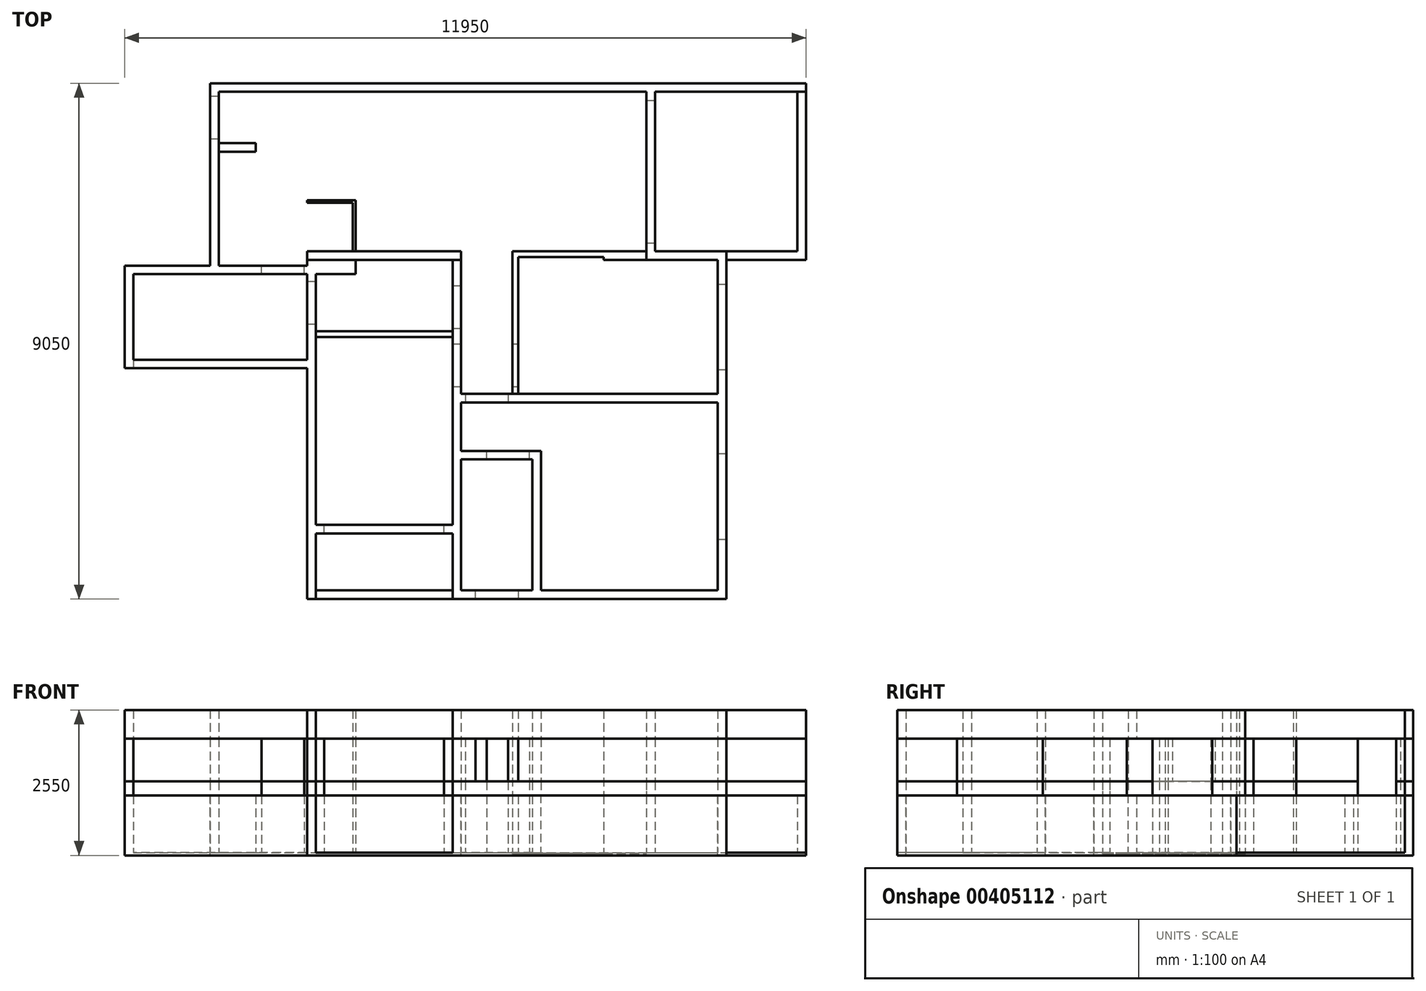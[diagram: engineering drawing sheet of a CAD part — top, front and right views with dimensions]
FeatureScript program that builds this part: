
annotation { "Feature Type Name" : "Feature", "Feature Type Description" : "" }
export const myFeature = defineFeature(function(context is Context, id is Id, definition is map)
    precondition{}
    {
        {
            var Q0;
            Q0=qCreatedBy(makeId("Top.planeOp"),FACE);
            var sketch = newSketch(context, id + "F0", { "sketchPlane" : qUnion([Q0])});
            skLineSegment(sketch, "E0.bottom", {"start": v(-5150, 2800) * mm, "end": v(2350, 2800) * mm});
            skLineSegment(sketch, "E0.top", {"start": v(-3600, 0) * mm, "end": v(-900, 0) * mm});
            skLineSegment(sketch, "E0.left", {"start": v(-5150, 2800) * mm, "end": v(-5150, 0) * mm});
            skLineSegment(sketch, "E0.right", {"start": v(5000, 2800) * mm, "end": v(5000, 0) * mm});
            skLineSegment(sketch, "E1.bottom", {"start": v(-5300, 2950) * mm, "end": v(5150, 2950) * mm});
            skLineSegment(sketch, "E1.top", {"start": v(-5300, -150) * mm, "end": v(-5150, -150) * mm});
            skLineSegment(sketch, "E1.left", {"start": v(-5300, 2950) * mm, "end": v(-5300, -150) * mm});
            skLineSegment(sketch, "E1.right", {"start": v(5150, 2950) * mm, "end": v(5150, -150) * mm});
            skLineSegment(sketch, "E2.top", {"start": v(2350, 2650) * mm, "end": v(2500, 2650) * mm});
            skLineSegment(sketch, "E2.left", {"start": v(2350, 2800) * mm, "end": v(2350, 2650) * mm});
            skLineSegment(sketch, "E2.right", {"start": v(2500, 2800) * mm, "end": v(2500, 2650) * mm});
            skLineSegment(sketch, "E3.top", {"start": v(2350, 150) * mm, "end": v(2500, 150) * mm});
            skLineSegment(sketch, "E3.left", {"start": v(2350, 2650) * mm, "end": v(2350, 150) * mm});
            skLineSegment(sketch, "E3.right", {"start": v(2500, 2650) * mm, "end": v(2500, 150) * mm});
            skLineSegment(sketch, "E4.left", {"start": v(2350, 150) * mm, "end": v(2350, 0) * mm});
            skLineSegment(sketch, "E4.right", {"start": v(2500, 150) * mm, "end": v(2500, 0) * mm});
            skLineSegment(sketch, "E5.bottom", {"start": v(0, 0) * mm, "end": v(2350, 0) * mm});
            skLineSegment(sketch, "E5.top", {"start": v(0, -2650) * mm, "end": v(3600, -2650) * mm});
            skLineSegment(sketch, "E5.left", {"start": v(0, 0) * mm, "end": v(0, -2650) * mm});
            skLineSegment(sketch, "E5.right", {"start": v(3750, 0) * mm, "end": v(3750, -2650) * mm});
            skLineSegment(sketch, "E6.bottom", {"start": v(100, -2500) * mm, "end": v(3600, -2500) * mm});
            skLineSegment(sketch, "E6.top", {"start": v(100, -100) * mm, "end": v(1600, -100) * mm});
            skLineSegment(sketch, "E6.left", {"start": v(100, -2500) * mm, "end": v(100, -100) * mm});
            skLineSegment(sketch, "E6.right", {"start": v(3600, -2500) * mm, "end": v(3600, -150) * mm});
            skLineSegment(sketch, "E7", {"start": v(1600, -100) * mm, "end": v(1600, -150) * mm});
            skLineSegment(sketch, "E8.trimOffspring", {"start": v(1600, -150) * mm, "end": v(3600, -150) * mm});
            skLineSegment(sketch, "E9.trimOffspring", {"start": v(2500, 2800) * mm, "end": v(5000, 2800) * mm});
            skLineSegment(sketch, "E10.trimOffspring", {"start": v(2500, 0) * mm, "end": v(3750, 0) * mm});
            skLineSegment(sketch, "E11.trimOffspring", {"start": v(2500, 0) * mm, "end": v(5000, 0) * mm});
            skLineSegment(sketch, "E12.trimOffspring", {"start": v(3750, -150) * mm, "end": v(5150, -150) * mm});
            skLineSegment(sketch, "E13.bottom", {"start": v(3600, -2500) * mm, "end": v(-1050, -2500) * mm});
            skLineSegment(sketch, "E13.top", {"start": v(3750, -6100) * mm, "end": v(-1050, -6100) * mm});
            skLineSegment(sketch, "E13.left", {"start": v(3750, -2500) * mm, "end": v(3750, -6100) * mm});
            skLineSegment(sketch, "E13.right", {"start": v(-1050, -2500) * mm, "end": v(-1050, -4800) * mm});
            skLineSegment(sketch, "E14.bottom", {"start": v(3600, -2650) * mm, "end": v(-900, -2650) * mm});
            skLineSegment(sketch, "E14.top", {"start": v(3600, -5950) * mm, "end": v(-900, -5950) * mm});
            skLineSegment(sketch, "E14.left", {"start": v(3600, -2650) * mm, "end": v(3600, -5950) * mm});
            skLineSegment(sketch, "E14.right", {"start": v(-900, -2650) * mm, "end": v(-900, -5950) * mm});
            skLineSegment(sketch, "E15.bottom", {"start": v(-900, -6100) * mm, "end": v(-3600, -6100) * mm});
            skLineSegment(sketch, "E15.top", {"start": v(-900, 0) * mm, "end": v(-3600, 0) * mm});
            skLineSegment(sketch, "E15.left", {"start": v(-900, -6100) * mm, "end": v(-900, 0) * mm});
            skLineSegment(sketch, "E15.right", {"start": v(-3600, -6100) * mm, "end": v(-3600, 0) * mm});
            skLineSegment(sketch, "E16.bottom", {"start": v(-1050, -5950) * mm, "end": v(-3450, -5950) * mm});
            skLineSegment(sketch, "E16.top", {"start": v(-1050, -150) * mm, "end": v(-3450, -150) * mm});
            skLineSegment(sketch, "E16.left", {"start": v(-1050, -5950) * mm, "end": v(-1050, -4950) * mm});
            skLineSegment(sketch, "E16.right", {"start": v(-3450, -5950) * mm, "end": v(-3450, -4950) * mm});
            skLineSegment(sketch, "E17.bottom", {"start": v(-1050, -1400) * mm, "end": v(-3450, -1400) * mm});
            skLineSegment(sketch, "E17.top", {"start": v(-1050, -1500) * mm, "end": v(-3450, -1500) * mm});
            skLineSegment(sketch, "E17.left", {"start": v(-1050, -1400) * mm, "end": v(-1050, -1500) * mm});
            skLineSegment(sketch, "E17.right", {"start": v(-3450, -1400) * mm, "end": v(-3450, -1500) * mm});
            skLineSegment(sketch, "E18.bottom", {"start": v(-3450, -4950) * mm, "end": v(-3300, -4950) * mm});
            skLineSegment(sketch, "E18.top", {"start": v(-3450, -4800) * mm, "end": v(-3300, -4800) * mm});
            skLineSegment(sketch, "E18.right", {"start": v(-3300, -4950) * mm, "end": v(-3300, -4800) * mm});
            skLineSegment(sketch, "E19.bottom", {"start": v(-3300, -4950) * mm, "end": v(-1200, -4950) * mm});
            skLineSegment(sketch, "E19.top", {"start": v(-3300, -4800) * mm, "end": v(-1200, -4800) * mm});
            skLineSegment(sketch, "E19.right", {"start": v(-1200, -4950) * mm, "end": v(-1200, -4800) * mm});
            skLineSegment(sketch, "E20.bottom", {"start": v(-1200, -4950) * mm, "end": v(-1050, -4950) * mm});
            skLineSegment(sketch, "E20.top", {"start": v(-1200, -4800) * mm, "end": v(-1050, -4800) * mm});
            skLineSegment(sketch, "E21.trimOffspring", {"start": v(-3450, -4800) * mm, "end": v(-3450, -150) * mm});
            skLineSegment(sketch, "E22.trimOffspring", {"start": v(-1050, -4950) * mm, "end": v(-1050, -6100) * mm});
            skLineSegment(sketch, "E23.trimOffspring", {"start": v(-1050, -4800) * mm, "end": v(-1050, -150) * mm});
            skLineSegment(sketch, "E24.trimOffspring", {"start": v(0, -150) * mm, "end": v(100, -150) * mm});
            skLineSegment(sketch, "E25.bottom", {"start": v(-5150, 1750) * mm, "end": v(-4500, 1750) * mm});
            skLineSegment(sketch, "E25.top", {"start": v(-5150, -250) * mm, "end": v(-2750, -250) * mm});
            skLineSegment(sketch, "E25.left", {"start": v(-5150, 1750) * mm, "end": v(-5150, -250) * mm});
            skLineSegment(sketch, "E25.right", {"start": v(-2750, 1750) * mm, "end": v(-2750, -250) * mm});
            skLineSegment(sketch, "E26.bottom", {"start": v(-5300, 1900) * mm, "end": v(-2750, 1900) * mm});
            skLineSegment(sketch, "E26.top", {"start": v(-5300, -400) * mm, "end": v(-2750, -400) * mm});
            skLineSegment(sketch, "E26.left", {"start": v(-5300, 1900) * mm, "end": v(-5300, -400) * mm});
            skLineSegment(sketch, "E26.right", {"start": v(-2750, 1900) * mm, "end": v(-2750, -400) * mm});
            skLineSegment(sketch, "E27", {"start": v(-4500, 1750) * mm, "end": v(-4500, 1900) * mm});
            skLineSegment(sketch, "E28.trimOffspring", {"start": v(-3600, -150) * mm, "end": v(-900, -150) * mm});
            skLineSegment(sketch, "E29.bottom", {"start": v(-3600, -400) * mm, "end": v(-6650, -400) * mm});
            skLineSegment(sketch, "E29.top", {"start": v(-3600, -1900) * mm, "end": v(-6650, -1900) * mm});
            skLineSegment(sketch, "E29.left", {"start": v(-3600, -400) * mm, "end": v(-3600, -1900) * mm});
            skLineSegment(sketch, "E29.right", {"start": v(-6650, -400) * mm, "end": v(-6650, -1900) * mm});
            skLineSegment(sketch, "E30.bottom", {"start": v(-3600, -400) * mm, "end": v(-6800, -400) * mm});
            skLineSegment(sketch, "E30.top", {"start": v(-3600, -2050) * mm, "end": v(-6800, -2050) * mm});
            skLineSegment(sketch, "E30.left", {"start": v(-3600, -400) * mm, "end": v(-3600, -2050) * mm});
            skLineSegment(sketch, "E30.right", {"start": v(-6800, -400) * mm, "end": v(-6800, -2050) * mm});
            skLineSegment(sketch, "E31", {"start": v(-2750, 900) * mm, "end": v(-3600, 900) * mm});
            skLineSegment(sketch, "E32", {"start": v(-3600, 900) * mm, "end": v(-3600, 850) * mm});
            skLineSegment(sketch, "E33", {"start": v(-3600, 850) * mm, "end": v(-2800, 850) * mm});
            skLineSegment(sketch, "E34", {"start": v(-2800, 850) * mm, "end": v(-2800, 0) * mm});
            skLineSegment(sketch, "E35.bottom", {"start": v(-900, -5950) * mm, "end": v(350, -5950) * mm});
            skLineSegment(sketch, "E35.top", {"start": v(-900, -3650) * mm, "end": v(350, -3650) * mm});
            skLineSegment(sketch, "E35.left", {"start": v(-900, -5950) * mm, "end": v(-900, -3650) * mm});
            skLineSegment(sketch, "E35.right", {"start": v(350, -5950) * mm, "end": v(350, -3650) * mm});
            skLineSegment(sketch, "E36.bottom", {"start": v(-900, -5950) * mm, "end": v(500, -5950) * mm});
            skLineSegment(sketch, "E36.top", {"start": v(-900, -3500) * mm, "end": v(500, -3500) * mm});
            skLineSegment(sketch, "E36.left", {"start": v(-900, -5950) * mm, "end": v(-900, -3500) * mm});
            skLineSegment(sketch, "E36.right", {"start": v(500, -5950) * mm, "end": v(500, -3500) * mm});
            skLineSegment(sketch, "E37", {"start": v(2350, 0) * mm, "end": v(2350, -150) * mm});
            skLineSegment(sketch, "E38", {"start": v(5000, 2800) * mm, "end": v(5150, 2800) * mm});
            skLineSegment(sketch, "E39.bottom", {"start": v(-6800, -400) * mm, "end": v(-5300, -400) * mm});
            skLineSegment(sketch, "E39.top", {"start": v(-6800, -250) * mm, "end": v(-5300, -250) * mm});
            skLineSegment(sketch, "E39.left", {"start": v(-6800, -400) * mm, "end": v(-6800, -250) * mm});
            skLineSegment(sketch, "E39.right", {"start": v(-5300, -400) * mm, "end": v(-5300, -250) * mm});
            skLineSegment(sketch, "E40", {"start": v(-3450, -5950) * mm, "end": v(-3450, -6100) * mm});
            skLineSegment(sketch, "E41", {"start": v(-6650, -1900) * mm, "end": v(-6650, -2050) * mm});
            skLineSegment(sketch, "E42", {"start": v(3600, -5050) * mm, "end": v(3750, -5050) * mm});
            skLineSegment(sketch, "E43", {"start": v(3600, -3550) * mm, "end": v(3750, -3550) * mm});
            skLineSegment(sketch, "E44", {"start": v(3600, -575) * mm, "end": v(3750, -575) * mm});
            skLineSegment(sketch, "E45", {"start": v(3600, -2075) * mm, "end": v(3750, -2075) * mm});
            skLineSegment(sketch, "E46", {"start": v(3600, -4300) * mm, "end": v(3750, -4300) * mm, "construction": true});
            skLineSegment(sketch, "E47", {"start": v(3600, -1325) * mm, "end": v(3750, -1325) * mm, "construction": true});
            skLineSegment(sketch, "E48", {"start": v(-825, -2500) * mm, "end": v(-825, -2650) * mm});
            skLineSegment(sketch, "E49", {"start": v(-75, -2500) * mm, "end": v(-75, -2650) * mm});
            skLineSegment(sketch, "E50", {"start": v(-450, -2500) * mm, "end": v(-450, -2650) * mm, "construction": true});
            skLineSegment(sketch, "E51", {"start": v(300, -3650) * mm, "end": v(300, -3500) * mm});
            skLineSegment(sketch, "E52", {"start": v(-450, -3650) * mm, "end": v(-450, -3500) * mm});
            skLineSegment(sketch, "E53", {"start": v(-1050, -1625) * mm, "end": v(-900, -1625) * mm});
            skLineSegment(sketch, "E54", {"start": v(-1050, -2375) * mm, "end": v(-900, -2375) * mm});
            skLineSegment(sketch, "E55", {"start": v(-1050, -1350) * mm, "end": v(-900, -1350) * mm});
            skLineSegment(sketch, "E56", {"start": v(-1050, -600) * mm, "end": v(-900, -600) * mm});
            skLineSegment(sketch, "E57", {"start": v(-3600, -525) * mm, "end": v(-3450, -525) * mm});
            skLineSegment(sketch, "E58", {"start": v(-3600, -1275) * mm, "end": v(-3450, -1275) * mm});
            skLineSegment(sketch, "E59", {"start": v(-650, -6100) * mm, "end": v(-650, -5950) * mm});
            skLineSegment(sketch, "E60", {"start": v(-3600, -900) * mm, "end": v(-3450, -900) * mm, "construction": true});
            skLineSegment(sketch, "E61", {"start": v(-275, -5950) * mm, "end": v(-275, -6100) * mm, "construction": true});
            skLineSegment(sketch, "E62", {"start": v(100, -5950) * mm, "end": v(100, -6100) * mm});
            skLineSegment(sketch, "E63", {"start": v(-5300, 1975) * mm, "end": v(-5150, 1975) * mm});
            skLineSegment(sketch, "E64", {"start": v(-5300, 2725) * mm, "end": v(-5150, 2725) * mm});
            skLineSegment(sketch, "E65", {"start": v(-5300, 2350) * mm, "end": v(-5150, 2350) * mm, "construction": true});
            skLineSegment(sketch, "E66", {"start": v(0, -2375) * mm, "end": v(100, -2375) * mm});
            skLineSegment(sketch, "E67", {"start": v(0, -1625) * mm, "end": v(100, -1625) * mm});
            skLineSegment(sketch, "E68", {"start": v(-3650, -400) * mm, "end": v(-3650, -250) * mm});
            skLineSegment(sketch, "E69", {"start": v(-4400, -400) * mm, "end": v(-4400, -250) * mm});
            skLineSegment(sketch, "E70", {"start": v(-1050, -2000) * mm, "end": v(-900, -2000) * mm, "construction": true});
            skSolve(sketch);
        }
        {
            var Q0;
            {var subQ1=sQuery(id+"F0.wireOp",EDGE,"E14.top");Q0=makeQuery(id+"F0.imprint","IMPRINT",FACE,{"disambiguationData":[TD([[makeQuery(id+"F0.imprint","IMPRINT",EDGE,{"derivedFrom":subQ1}),1.0]])]});}
            var Q1;
            {var subQ0=sQuery(id+"F0.wireOp",EDGE,"E42");Q1=makeQuery(id+"F0.imprint","IMPRINT",FACE,{"disambiguationData":[TD([[makeQuery(id+"F0.imprint","IMPRINT",EDGE,{"derivedFrom":subQ0}),1.0]])]});}
            var Q2;
            {var subQ7=sQuery(id+"F0.wireOp",EDGE,"E43");Q2=makeQuery(id+"F0.imprint","IMPRINT",FACE,{"disambiguationData":[TD([[makeQuery(id+"F0.imprint","IMPRINT",EDGE,{"derivedFrom":subQ7}),1.0]])]});}
            var Q3;
            {var subQ1=sQuery(id+"F0.wireOp",EDGE,"E14.top");Q3=makeQuery(id+"F0.imprint","IMPRINT",FACE,{"disambiguationData":[TD([[makeQuery(id+"F0.imprint","IMPRINT",EDGE,{"derivedFrom":subQ1}),-1.0]])]});}
            var Q4;
            {var subQ3=sQuery(id+"F0.wireOp",EDGE,"E35.right");Q4=makeQuery(id+"F0.imprint","IMPRINT",FACE,{"disambiguationData":[TD([[makeQuery(id+"F0.imprint","IMPRINT",EDGE,{"derivedFrom":subQ3}),-1.0]])]});}
            var Q5;
            {var subQ0=sQuery(id+"F0.wireOp",EDGE,"E51");Q5=makeQuery(id+"F0.imprint","IMPRINT",FACE,{"disambiguationData":[TD([[makeQuery(id+"F0.imprint","IMPRINT",EDGE,{"derivedFrom":subQ0}),1.0]])]});}
            var Q6;
            {var subQ3=sQuery(id+"F0.wireOp",EDGE,"E52");Q6=makeQuery(id+"F0.imprint","IMPRINT",FACE,{"disambiguationData":[TD([[makeQuery(id+"F0.imprint","IMPRINT",EDGE,{"derivedFrom":subQ3}),1.0]])]});}
            var Q7;
            {var subQ0=sQuery(id+"F0.wireOp",EDGE,"E59");Q7=makeQuery(id+"F0.imprint","IMPRINT",FACE,{"disambiguationData":[TD([[makeQuery(id+"F0.imprint","IMPRINT",EDGE,{"derivedFrom":subQ0}),-1.0]])]});}
            var Q8;
            {var subQ3=sQuery(id+"F0.wireOp",EDGE,"E59");Q8=makeQuery(id+"F0.imprint","IMPRINT",FACE,{"disambiguationData":[TD([[makeQuery(id+"F0.imprint","IMPRINT",EDGE,{"derivedFrom":subQ3}),1.0]])]});}
            var Q9;
            {var subQ2=sQuery(id+"F0.wireOp",EDGE,"E20.bottom");Q9=makeQuery(id+"F0.imprint","IMPRINT",FACE,{"disambiguationData":[TD([[makeQuery(id+"F0.imprint","IMPRINT",EDGE,{"derivedFrom":subQ2}),1.0]])]});}
            var Q10;
            Q10=makeQuery(id+"F0.imprint","IMPRINT",FACE,{"disambiguationData":[TD([[makeQuery(id+"F0.imprint","IMPRINT",EDGE,{"derivedFrom":sQuery(id+"F0.wireOp",EDGE,"E19.bottom")}),1.0]])]});
            var Q11;
            Q11=makeQuery(id+"F0.imprint","IMPRINT",FACE,{"disambiguationData":[TD([[makeQuery(id+"F0.imprint","IMPRINT",EDGE,{"derivedFrom":sQuery(id+"F0.wireOp",EDGE,"E16.right")}),1.0]])]});
            var Q12;
            {var subQ4=sQuery(id+"F0.wireOp",EDGE,"E17.top");Q12=makeQuery(id+"F0.imprint","IMPRINT",FACE,{"disambiguationData":[TD([[makeQuery(id+"F0.imprint","IMPRINT",EDGE,{"derivedFrom":subQ4}),1.0]])]});}
            var Q13;
            {var subQ5=sQuery(id+"F0.wireOp",EDGE,"E54");Q13=makeQuery(id+"F0.imprint","IMPRINT",FACE,{"disambiguationData":[TD([[makeQuery(id+"F0.imprint","IMPRINT",EDGE,{"derivedFrom":subQ5}),-1.0]])]});}
            var Q14;
            {var subQ0=sQuery(id+"F0.wireOp",EDGE,"E48");Q14=makeQuery(id+"F0.imprint","IMPRINT",FACE,{"disambiguationData":[TD([[makeQuery(id+"F0.imprint","IMPRINT",EDGE,{"derivedFrom":subQ0}),-1.0]])]});}
            var Q15;
            {var subQ0=sQuery(id+"F0.wireOp",EDGE,"E48");Q15=makeQuery(id+"F0.imprint","IMPRINT",FACE,{"disambiguationData":[TD([[makeQuery(id+"F0.imprint","IMPRINT",EDGE,{"derivedFrom":subQ0}),1.0]])]});}
            var Q16;
            {var subQ5=sQuery(id+"F0.wireOp",EDGE,"E49");Q16=makeQuery(id+"F0.imprint","IMPRINT",FACE,{"disambiguationData":[TD([[makeQuery(id+"F0.imprint","IMPRINT",EDGE,{"derivedFrom":subQ5}),1.0]])]});}
            var Q17;
            {var subQ0=sQuery(id+"F0.wireOp",EDGE,"E53");Q17=makeQuery(id+"F0.imprint","IMPRINT",FACE,{"disambiguationData":[TD([[makeQuery(id+"F0.imprint","IMPRINT",EDGE,{"derivedFrom":subQ0}),-1.0]])]});}
            var Q18;
            {var subQ4=sQuery(id+"F0.wireOp",EDGE,"E53");Q18=makeQuery(id+"F0.imprint","IMPRINT",FACE,{"disambiguationData":[TD([[makeQuery(id+"F0.imprint","IMPRINT",EDGE,{"derivedFrom":subQ4}),1.0]])]});}
            var Q19;
            {var subQ0=sQuery(id+"F0.wireOp",EDGE,"E55");Q19=makeQuery(id+"F0.imprint","IMPRINT",FACE,{"disambiguationData":[TD([[makeQuery(id+"F0.imprint","IMPRINT",EDGE,{"derivedFrom":subQ0}),1.0]])]});}
            var Q20;
            {var subQ0=sQuery(id+"F0.wireOp",EDGE,"E17.bottom");Q20=makeQuery(id+"F0.imprint","IMPRINT",FACE,{"disambiguationData":[TD([[makeQuery(id+"F0.imprint","IMPRINT",EDGE,{"derivedFrom":subQ0}),1.0]])]});}
            var Q21;
            {var subQ3=sQuery(id+"F0.wireOp",EDGE,"E56");Q21=makeQuery(id+"F0.imprint","IMPRINT",FACE,{"disambiguationData":[TD([[makeQuery(id+"F0.imprint","IMPRINT",EDGE,{"derivedFrom":subQ3}),1.0]])]});}
            var Q22;
            {var subQ1=sQuery(id+"F0.wireOp",EDGE,"E15.top");var subQ5=sQuery(id+"F0.wireOp",EDGE,"E15.left");var subQ6=makeQuery(id+"F0.imprint","INTERSECT",VERTEX,{"derivedFrom":[subQ1,subQ5]});Q22=makeQuery(id+"F0.imprint","IMPRINT",FACE,{"disambiguationData":[TD([[makeQuery(id+"F0.imprint","IMPRINT",EDGE,{"disambiguationData":[TD([[subQ6,-1.0]])],"derivedFrom":subQ1}),1.0]])]});}
            var Q23;
            {var subQ0=sQuery(id+"F0.wireOp",EDGE,"E57");Q23=makeQuery(id+"F0.imprint","IMPRINT",FACE,{"disambiguationData":[TD([[makeQuery(id+"F0.imprint","IMPRINT",EDGE,{"derivedFrom":subQ0}),-1.0]])]});}
            var Q24;
            {var subQ0=sQuery(id+"F0.wireOp",EDGE,"E57");Q24=makeQuery(id+"F0.imprint","IMPRINT",FACE,{"disambiguationData":[TD([[makeQuery(id+"F0.imprint","IMPRINT",EDGE,{"derivedFrom":subQ0}),1.0]])]});}
            var Q25;
            {var subQ0=sQuery(id+"F0.wireOp",EDGE,"E26.top");var subQ5=sQuery(id+"F0.wireOp",EDGE,"E21.trimOffspring");var subQ6=makeQuery(id+"F0.imprint","INTERSECT",VERTEX,{"derivedFrom":[subQ5,subQ0]});Q25=makeQuery(id+"F0.imprint","IMPRINT",FACE,{"disambiguationData":[TD([[makeQuery(id+"F0.imprint","IMPRINT",EDGE,{"disambiguationData":[TD([[subQ6,-1.0]])],"derivedFrom":subQ5}),1.0]])]});}
            var Q26;
            {var subQ0=sQuery(id+"F0.wireOp",EDGE,"E26.top");var subQ1=sQuery(id+"F0.wireOp",EDGE,"E21.trimOffspring");var subQ2=makeQuery(id+"F0.imprint","INTERSECT",VERTEX,{"derivedFrom":[subQ1,subQ0]});Q26=makeQuery(id+"F0.imprint","IMPRINT",FACE,{"disambiguationData":[TD([[makeQuery(id+"F0.imprint","IMPRINT",EDGE,{"disambiguationData":[TD([[subQ2,-1.0]])],"derivedFrom":subQ1}),-1.0]])]});}
            var Q27;
            {var subQ0=sQuery(id+"F0.wireOp",EDGE,"E28.trimOffspring");var subQ1=sQuery(id+"F0.wireOp",EDGE,"E21.trimOffspring");var subQ2=makeQuery(id+"F0.imprint","INTERSECT",VERTEX,{"derivedFrom":[subQ1,subQ0]});Q27=makeQuery(id+"F0.imprint","IMPRINT",FACE,{"disambiguationData":[TD([[makeQuery(id+"F0.imprint","IMPRINT",EDGE,{"disambiguationData":[TD([[subQ2,1.0]])],"derivedFrom":subQ1}),-1.0]])]});}
            var Q28;
            {var subQ1=sQuery(id+"F0.wireOp",EDGE,"E15.top");var subQ8=makeQuery(id+"F0.imprint","INTERSECT",VERTEX,{"derivedFrom":[subQ1,sQuery(id+"F0.wireOp",EDGE,"E34")]});Q28=makeQuery(id+"F0.imprint","IMPRINT",FACE,{"disambiguationData":[TD([[makeQuery(id+"F0.imprint","IMPRINT",EDGE,{"disambiguationData":[TD([[subQ8,1.0]])],"derivedFrom":subQ1}),1.0]])]});}
            var Q29;
            {var subQ0=sQuery(id+"F0.wireOp",EDGE,"E28.trimOffspring");var subQ1=sQuery(id+"F0.wireOp",EDGE,"E15.right");var subQ2=makeQuery(id+"F0.imprint","INTERSECT",VERTEX,{"derivedFrom":[subQ1,subQ0]});Q29=makeQuery(id+"F0.imprint","IMPRINT",FACE,{"disambiguationData":[TD([[makeQuery(id+"F0.imprint","IMPRINT",EDGE,{"disambiguationData":[TD([[subQ2,1.0]])],"derivedFrom":subQ1}),-1.0]])]});}
            var Q30;
            {var subQ1=sQuery(id+"F0.wireOp",EDGE,"E1.top");Q30=makeQuery(id+"F0.imprint","IMPRINT",FACE,{"disambiguationData":[TD([[makeQuery(id+"F0.imprint","IMPRINT",EDGE,{"derivedFrom":subQ1}),-1.0]])]});}
            var Q31;
            Q31=makeQuery(id+"F0.imprint","IMPRINT",FACE,{"disambiguationData":[TD([[makeQuery(id+"F0.imprint","IMPRINT",EDGE,{"derivedFrom":sQuery(id+"F0.wireOp",EDGE,"E39.top")}),-1.0]])]});
            var Q32;
            {var subQ1=sQuery(id+"F0.wireOp",EDGE,"E29.right");Q32=makeQuery(id+"F0.imprint","IMPRINT",FACE,{"disambiguationData":[TD([[makeQuery(id+"F0.imprint","IMPRINT",EDGE,{"derivedFrom":subQ1}),-1.0]])]});}
            var Q33;
            {var subQ1=sQuery(id+"F0.wireOp",EDGE,"E1.top");Q33=makeQuery(id+"F0.imprint","IMPRINT",FACE,{"disambiguationData":[TD([[makeQuery(id+"F0.imprint","IMPRINT",EDGE,{"derivedFrom":subQ1}),1.0]])]});}
            var Q34;
            {var subQ0=sQuery(id+"F0.wireOp",EDGE,"E63");Q34=makeQuery(id+"F0.imprint","IMPRINT",FACE,{"disambiguationData":[TD([[makeQuery(id+"F0.imprint","IMPRINT",EDGE,{"derivedFrom":subQ0}),-1.0]])]});}
            var Q35;
            {var subQ0=sQuery(id+"F0.wireOp",EDGE,"E63");Q35=makeQuery(id+"F0.imprint","IMPRINT",FACE,{"disambiguationData":[TD([[makeQuery(id+"F0.imprint","IMPRINT",EDGE,{"derivedFrom":subQ0}),1.0]])]});}
            var Q36;
            {var subQ5=sQuery(id+"F0.wireOp",EDGE,"E0.bottom");Q36=makeQuery(id+"F0.imprint","IMPRINT",FACE,{"disambiguationData":[TD([[makeQuery(id+"F0.imprint","IMPRINT",EDGE,{"derivedFrom":subQ5}),1.0]])]});}
            var Q37;
            Q37=makeQuery(id+"F0.imprint","IMPRINT",FACE,{"disambiguationData":[TD([[makeQuery(id+"F0.imprint","IMPRINT",EDGE,{"derivedFrom":sQuery(id+"F0.wireOp",EDGE,"E2.top")}),-1.0]])]});
            var Q38;
            {var subQ0=sQuery(id+"F0.wireOp",EDGE,"E44");Q38=makeQuery(id+"F0.imprint","IMPRINT",FACE,{"disambiguationData":[TD([[makeQuery(id+"F0.imprint","IMPRINT",EDGE,{"derivedFrom":subQ0}),-1.0]])]});}
            var Q39;
            Q39=makeQuery(id+"F0.imprint","IMPRINT",FACE,{"disambiguationData":[TD([[makeQuery(id+"F0.imprint","IMPRINT",EDGE,{"derivedFrom":sQuery(id+"F0.wireOp",EDGE,"E3.top")}),-1.0]])]});
            var Q40;
            {var subQ0=sQuery(id+"F0.wireOp",EDGE,"E35.right");Q40=makeQuery(id+"F0.imprint","IMPRINT",FACE,{"disambiguationData":[TD([[makeQuery(id+"F0.imprint","IMPRINT",EDGE,{"derivedFrom":subQ0}),1.0]])]});}
            var Q41;
            {var subQ0=sQuery(id+"F0.wireOp",EDGE,"E16.bottom");Q41=makeQuery(id+"F0.imprint","IMPRINT",FACE,{"disambiguationData":[TD([[makeQuery(id+"F0.imprint","IMPRINT",EDGE,{"derivedFrom":subQ0}),-1.0]])]});}
            var Q42;
            {var subQ4=sQuery(id+"F0.wireOp",EDGE,"E16.bottom");Q42=makeQuery(id+"F0.imprint","IMPRINT",FACE,{"disambiguationData":[TD([[makeQuery(id+"F0.imprint","IMPRINT",EDGE,{"derivedFrom":subQ4}),1.0]])]});}
            var Q43;
            {var subQ4=sQuery(id+"F0.wireOp",EDGE,"E29.top");Q43=makeQuery(id+"F0.imprint","IMPRINT",FACE,{"disambiguationData":[TD([[makeQuery(id+"F0.imprint","IMPRINT",EDGE,{"derivedFrom":subQ4}),-1.0]])]});}
            var Q44;
            {var subQ0=sQuery(id+"F0.wireOp",EDGE,"E29.top");Q44=makeQuery(id+"F0.imprint","IMPRINT",FACE,{"disambiguationData":[TD([[makeQuery(id+"F0.imprint","IMPRINT",EDGE,{"derivedFrom":subQ0}),1.0]])]});}
            var Q45;
            {var subQ11=sQuery(id+"F0.wireOp",EDGE,"E17.bottom");Q45=makeQuery(id+"F0.imprint","IMPRINT",FACE,{"disambiguationData":[TD([[makeQuery(id+"F0.imprint","IMPRINT",EDGE,{"derivedFrom":subQ11}),-1.0]])]});}
            var Q46;
            {var subQ10=sQuery(id+"F0.wireOp",EDGE,"E6.top");Q46=makeQuery(id+"F0.imprint","IMPRINT",FACE,{"disambiguationData":[TD([[makeQuery(id+"F0.imprint","IMPRINT",EDGE,{"derivedFrom":subQ10}),-1.0]])]});}
            var Q47;
            {var subQ20=sQuery(id+"F0.wireOp",EDGE,"E0.bottom");Q47=makeQuery(id+"F0.imprint","IMPRINT",FACE,{"disambiguationData":[TD([[makeQuery(id+"F0.imprint","IMPRINT",EDGE,{"derivedFrom":subQ20}),-1.0]])]});}
            var Q48;
            {var subQ0=sQuery(id+"F0.wireOp",EDGE,"E66");Q48=makeQuery(id+"F0.imprint","IMPRINT",FACE,{"disambiguationData":[TD([[makeQuery(id+"F0.imprint","IMPRINT",EDGE,{"derivedFrom":subQ0}),-1.0]])]});}
            var Q49;
            {var subQ0=sQuery(id+"F0.wireOp",EDGE,"E66");Q49=makeQuery(id+"F0.imprint","IMPRINT",FACE,{"disambiguationData":[TD([[makeQuery(id+"F0.imprint","IMPRINT",EDGE,{"derivedFrom":subQ0}),1.0]])]});}
            var Q50;
            {var subQ0=sQuery(id+"F0.wireOp",EDGE,"E24.trimOffspring");Q50=makeQuery(id+"F0.imprint","IMPRINT",FACE,{"disambiguationData":[TD([[makeQuery(id+"F0.imprint","IMPRINT",EDGE,{"derivedFrom":subQ0}),-1.0]])]});}
            var Q51;
            {var subQ2=sQuery(id+"F0.wireOp",EDGE,"E6.top");Q51=makeQuery(id+"F0.imprint","IMPRINT",FACE,{"disambiguationData":[TD([[makeQuery(id+"F0.imprint","IMPRINT",EDGE,{"derivedFrom":subQ2}),1.0]])]});}
            var Q52;
            {var subQ3=sQuery(id+"F0.wireOp",EDGE,"E0.right");Q52=makeQuery(id+"F0.imprint","IMPRINT",FACE,{"disambiguationData":[TD([[makeQuery(id+"F0.imprint","IMPRINT",EDGE,{"derivedFrom":subQ3}),-1.0]])]});}
            var Q53;
            {var subQ1=sQuery(id+"F0.wireOp",EDGE,"E0.right");Q53=makeQuery(id+"F0.imprint","IMPRINT",FACE,{"disambiguationData":[TD([[makeQuery(id+"F0.imprint","IMPRINT",EDGE,{"derivedFrom":subQ1}),1.0]])]});}
            var Q54;
            {var subQ14=sQuery(id+"F0.wireOp",EDGE,"E25.bottom");Q54=makeQuery(id+"F0.imprint","IMPRINT",FACE,{"disambiguationData":[TD([[makeQuery(id+"F0.imprint","IMPRINT",EDGE,{"derivedFrom":subQ14}),-1.0]])]});}
            var Q55;
            {var subQ0=sQuery(id+"F0.wireOp",EDGE,"E25.bottom");Q55=makeQuery(id+"F0.imprint","IMPRINT",FACE,{"disambiguationData":[TD([[makeQuery(id+"F0.imprint","IMPRINT",EDGE,{"derivedFrom":subQ0}),1.0]])]});}
            var Q56;
            {var subQ0=sQuery(id+"F0.wireOp",EDGE,"E31");Q56=makeQuery(id+"F0.imprint","IMPRINT",FACE,{"disambiguationData":[TD([[makeQuery(id+"F0.imprint","IMPRINT",EDGE,{"derivedFrom":subQ0}),1.0]])]});}
            var Q57;
            {var subQ0=sQuery(id+"F0.wireOp",EDGE,"E68");Q57=makeQuery(id+"F0.imprint","IMPRINT",FACE,{"disambiguationData":[TD([[makeQuery(id+"F0.imprint","IMPRINT",EDGE,{"derivedFrom":subQ0}),1.0]])]});}
            var Q58;
            {var subQ5=sQuery(id+"F0.wireOp",EDGE,"E68");Q58=makeQuery(id+"F0.imprint","IMPRINT",FACE,{"disambiguationData":[TD([[makeQuery(id+"F0.imprint","IMPRINT",EDGE,{"derivedFrom":subQ5}),-1.0]])]});}
            extrude(context, id + "F1", {"entities" : qUnion([Q0, Q1, Q2, Q3, Q4, Q5, Q6, Q7, Q8, Q9, Q10, Q11, Q12, Q13, Q14, Q15, Q16, Q17, Q18, Q19, Q20, Q21, Q22, Q23, Q24, Q25, Q26, Q27, Q28, Q29, Q30, Q31, Q32, Q33, Q34, Q35, Q36, Q37, Q38, Q39, Q40, Q41, Q42, Q43, Q44, Q45, Q46, Q47, Q48, Q49, Q50, Q51, Q52, Q53, Q54, Q55, Q56, Q57, Q58]), "oppositeDirection" : true, "depth" : 50 * mm});
        }
        {
            var Q0;
            {var subQ1=sQuery(id+"F0.wireOp",EDGE,"E14.top");Q0=makeQuery(id+"F0.imprint","IMPRINT",FACE,{"disambiguationData":[TD([[makeQuery(id+"F0.imprint","IMPRINT",EDGE,{"derivedFrom":subQ1}),1.0]])]});}
            var Q1;
            {var subQ0=sQuery(id+"F0.wireOp",EDGE,"E42");Q1=makeQuery(id+"F0.imprint","IMPRINT",FACE,{"disambiguationData":[TD([[makeQuery(id+"F0.imprint","IMPRINT",EDGE,{"derivedFrom":subQ0}),1.0]])]});}
            var Q2;
            {var subQ7=sQuery(id+"F0.wireOp",EDGE,"E43");Q2=makeQuery(id+"F0.imprint","IMPRINT",FACE,{"disambiguationData":[TD([[makeQuery(id+"F0.imprint","IMPRINT",EDGE,{"derivedFrom":subQ7}),1.0]])]});}
            var Q3;
            {var subQ0=sQuery(id+"F0.wireOp",EDGE,"E44");Q3=makeQuery(id+"F0.imprint","IMPRINT",FACE,{"disambiguationData":[TD([[makeQuery(id+"F0.imprint","IMPRINT",EDGE,{"derivedFrom":subQ0}),-1.0]])]});}
            var Q4;
            Q4=makeQuery(id+"F0.imprint","IMPRINT",FACE,{"disambiguationData":[TD([[makeQuery(id+"F0.imprint","IMPRINT",EDGE,{"derivedFrom":sQuery(id+"F0.wireOp",EDGE,"E3.top")}),-1.0]])]});
            var Q5;
            {var subQ4=sQuery(id+"F0.wireOp",EDGE,"E0.bottom");Q5=makeQuery(id+"F0.imprint","IMPRINT",FACE,{"disambiguationData":[TD([[makeQuery(id+"F0.imprint","IMPRINT",EDGE,{"derivedFrom":subQ4}),1.0]])]});}
            var Q6;
            {var subQ3=sQuery(id+"F0.wireOp",EDGE,"E35.right");Q6=makeQuery(id+"F0.imprint","IMPRINT",FACE,{"disambiguationData":[TD([[makeQuery(id+"F0.imprint","IMPRINT",EDGE,{"derivedFrom":subQ3}),-1.0]])]});}
            var Q7;
            {var subQ3=sQuery(id+"F0.wireOp",EDGE,"E52");Q7=makeQuery(id+"F0.imprint","IMPRINT",FACE,{"disambiguationData":[TD([[makeQuery(id+"F0.imprint","IMPRINT",EDGE,{"derivedFrom":subQ3}),1.0]])]});}
            var Q8;
            {var subQ2=sQuery(id+"F0.wireOp",EDGE,"E20.bottom");Q8=makeQuery(id+"F0.imprint","IMPRINT",FACE,{"disambiguationData":[TD([[makeQuery(id+"F0.imprint","IMPRINT",EDGE,{"derivedFrom":subQ2}),1.0]])]});}
            var Q9;
            {var subQ0=sQuery(id+"F0.wireOp",EDGE,"E59");Q9=makeQuery(id+"F0.imprint","IMPRINT",FACE,{"disambiguationData":[TD([[makeQuery(id+"F0.imprint","IMPRINT",EDGE,{"derivedFrom":subQ0}),-1.0]])]});}
            var Q10;
            {var subQ3=sQuery(id+"F0.wireOp",EDGE,"E59");Q10=makeQuery(id+"F0.imprint","IMPRINT",FACE,{"disambiguationData":[TD([[makeQuery(id+"F0.imprint","IMPRINT",EDGE,{"derivedFrom":subQ3}),1.0]])]});}
            var Q11;
            Q11=makeQuery(id+"F0.imprint","IMPRINT",FACE,{"disambiguationData":[TD([[makeQuery(id+"F0.imprint","IMPRINT",EDGE,{"derivedFrom":sQuery(id+"F0.wireOp",EDGE,"E16.right")}),1.0]])]});
            var Q12;
            {var subQ0=sQuery(id+"F0.wireOp",EDGE,"E48");Q12=makeQuery(id+"F0.imprint","IMPRINT",FACE,{"disambiguationData":[TD([[makeQuery(id+"F0.imprint","IMPRINT",EDGE,{"derivedFrom":subQ0}),-1.0]])]});}
            var Q13;
            {var subQ5=sQuery(id+"F0.wireOp",EDGE,"E54");Q13=makeQuery(id+"F0.imprint","IMPRINT",FACE,{"disambiguationData":[TD([[makeQuery(id+"F0.imprint","IMPRINT",EDGE,{"derivedFrom":subQ5}),-1.0]])]});}
            var Q14;
            {var subQ4=sQuery(id+"F0.wireOp",EDGE,"E53");Q14=makeQuery(id+"F0.imprint","IMPRINT",FACE,{"disambiguationData":[TD([[makeQuery(id+"F0.imprint","IMPRINT",EDGE,{"derivedFrom":subQ4}),1.0]])]});}
            var Q15;
            {var subQ0=sQuery(id+"F0.wireOp",EDGE,"E17.bottom");Q15=makeQuery(id+"F0.imprint","IMPRINT",FACE,{"disambiguationData":[TD([[makeQuery(id+"F0.imprint","IMPRINT",EDGE,{"derivedFrom":subQ0}),1.0]])]});}
            var Q16;
            {var subQ0=sQuery(id+"F0.wireOp",EDGE,"E57");Q16=makeQuery(id+"F0.imprint","IMPRINT",FACE,{"disambiguationData":[TD([[makeQuery(id+"F0.imprint","IMPRINT",EDGE,{"derivedFrom":subQ0}),-1.0]])]});}
            var Q17;
            {var subQ0=sQuery(id+"F0.wireOp",EDGE,"E57");Q17=makeQuery(id+"F0.imprint","IMPRINT",FACE,{"disambiguationData":[TD([[makeQuery(id+"F0.imprint","IMPRINT",EDGE,{"derivedFrom":subQ0}),1.0]])]});}
            var Q18;
            {var subQ0=sQuery(id+"F0.wireOp",EDGE,"E26.top");var subQ5=sQuery(id+"F0.wireOp",EDGE,"E21.trimOffspring");var subQ6=makeQuery(id+"F0.imprint","INTERSECT",VERTEX,{"derivedFrom":[subQ5,subQ0]});Q18=makeQuery(id+"F0.imprint","IMPRINT",FACE,{"disambiguationData":[TD([[makeQuery(id+"F0.imprint","IMPRINT",EDGE,{"disambiguationData":[TD([[subQ6,-1.0]])],"derivedFrom":subQ5}),1.0]])]});}
            var Q19;
            {var subQ0=sQuery(id+"F0.wireOp",EDGE,"E26.top");var subQ1=sQuery(id+"F0.wireOp",EDGE,"E21.trimOffspring");var subQ2=makeQuery(id+"F0.imprint","INTERSECT",VERTEX,{"derivedFrom":[subQ1,subQ0]});Q19=makeQuery(id+"F0.imprint","IMPRINT",FACE,{"disambiguationData":[TD([[makeQuery(id+"F0.imprint","IMPRINT",EDGE,{"disambiguationData":[TD([[subQ2,-1.0]])],"derivedFrom":subQ1}),-1.0]])]});}
            var Q20;
            {var subQ0=sQuery(id+"F0.wireOp",EDGE,"E28.trimOffspring");var subQ1=sQuery(id+"F0.wireOp",EDGE,"E21.trimOffspring");var subQ2=makeQuery(id+"F0.imprint","INTERSECT",VERTEX,{"derivedFrom":[subQ1,subQ0]});Q20=makeQuery(id+"F0.imprint","IMPRINT",FACE,{"disambiguationData":[TD([[makeQuery(id+"F0.imprint","IMPRINT",EDGE,{"disambiguationData":[TD([[subQ2,1.0]])],"derivedFrom":subQ1}),-1.0]])]});}
            var Q21;
            {var subQ1=sQuery(id+"F0.wireOp",EDGE,"E15.top");var subQ6=makeQuery(id+"F0.imprint","INTERSECT",VERTEX,{"derivedFrom":[subQ1,sQuery(id+"F0.wireOp",EDGE,"E34")]});Q21=makeQuery(id+"F0.imprint","IMPRINT",FACE,{"disambiguationData":[TD([[makeQuery(id+"F0.imprint","IMPRINT",EDGE,{"disambiguationData":[TD([[subQ6,1.0]])],"derivedFrom":subQ1}),1.0]])]});}
            var Q22;
            {var subQ0=sQuery(id+"F0.wireOp",EDGE,"E28.trimOffspring");var subQ1=sQuery(id+"F0.wireOp",EDGE,"E15.right");var subQ2=makeQuery(id+"F0.imprint","INTERSECT",VERTEX,{"derivedFrom":[subQ1,subQ0]});Q22=makeQuery(id+"F0.imprint","IMPRINT",FACE,{"disambiguationData":[TD([[makeQuery(id+"F0.imprint","IMPRINT",EDGE,{"disambiguationData":[TD([[subQ2,1.0]])],"derivedFrom":subQ1}),-1.0]])]});}
            var Q23;
            {var subQ5=sQuery(id+"F0.wireOp",EDGE,"E68");Q23=makeQuery(id+"F0.imprint","IMPRINT",FACE,{"disambiguationData":[TD([[makeQuery(id+"F0.imprint","IMPRINT",EDGE,{"derivedFrom":subQ5}),-1.0]])]});}
            var Q24;
            {var subQ1=sQuery(id+"F0.wireOp",EDGE,"E1.top");Q24=makeQuery(id+"F0.imprint","IMPRINT",FACE,{"disambiguationData":[TD([[makeQuery(id+"F0.imprint","IMPRINT",EDGE,{"derivedFrom":subQ1}),-1.0]])]});}
            var Q25;
            Q25=makeQuery(id+"F0.imprint","IMPRINT",FACE,{"disambiguationData":[TD([[makeQuery(id+"F0.imprint","IMPRINT",EDGE,{"derivedFrom":sQuery(id+"F0.wireOp",EDGE,"E39.top")}),-1.0]])]});
            var Q26;
            {var subQ0=sQuery(id+"F0.wireOp",EDGE,"E29.top");Q26=makeQuery(id+"F0.imprint","IMPRINT",FACE,{"disambiguationData":[TD([[makeQuery(id+"F0.imprint","IMPRINT",EDGE,{"derivedFrom":subQ0}),1.0]])]});}
            var Q27;
            {var subQ1=sQuery(id+"F0.wireOp",EDGE,"E29.right");Q27=makeQuery(id+"F0.imprint","IMPRINT",FACE,{"disambiguationData":[TD([[makeQuery(id+"F0.imprint","IMPRINT",EDGE,{"derivedFrom":subQ1}),-1.0]])]});}
            var Q28;
            {var subQ4=sQuery(id+"F0.wireOp",EDGE,"E1.top");Q28=makeQuery(id+"F0.imprint","IMPRINT",FACE,{"disambiguationData":[TD([[makeQuery(id+"F0.imprint","IMPRINT",EDGE,{"derivedFrom":subQ4}),1.0]])]});}
            var Q29;
            {var subQ0=sQuery(id+"F0.wireOp",EDGE,"E25.bottom");Q29=makeQuery(id+"F0.imprint","IMPRINT",FACE,{"disambiguationData":[TD([[makeQuery(id+"F0.imprint","IMPRINT",EDGE,{"derivedFrom":subQ0}),1.0]])]});}
            var Q30;
            {var subQ0=sQuery(id+"F0.wireOp",EDGE,"E63");Q30=makeQuery(id+"F0.imprint","IMPRINT",FACE,{"disambiguationData":[TD([[makeQuery(id+"F0.imprint","IMPRINT",EDGE,{"derivedFrom":subQ0}),-1.0]])]});}
            var Q31;
            {var subQ0=sQuery(id+"F0.wireOp",EDGE,"E31");Q31=makeQuery(id+"F0.imprint","IMPRINT",FACE,{"disambiguationData":[TD([[makeQuery(id+"F0.imprint","IMPRINT",EDGE,{"derivedFrom":subQ0}),1.0]])]});}
            var Q32;
            {var subQ3=sQuery(id+"F0.wireOp",EDGE,"E56");Q32=makeQuery(id+"F0.imprint","IMPRINT",FACE,{"disambiguationData":[TD([[makeQuery(id+"F0.imprint","IMPRINT",EDGE,{"derivedFrom":subQ3}),1.0]])]});}
            var Q33;
            {var subQ4=sQuery(id+"F0.wireOp",EDGE,"E15.top");var subQ6=sQuery(id+"F0.wireOp",EDGE,"E15.left");var subQ7=makeQuery(id+"F0.imprint","INTERSECT",VERTEX,{"derivedFrom":[subQ4,subQ6]});Q33=makeQuery(id+"F0.imprint","IMPRINT",FACE,{"disambiguationData":[TD([[makeQuery(id+"F0.imprint","IMPRINT",EDGE,{"disambiguationData":[TD([[subQ7,-1.0]])],"derivedFrom":subQ4}),1.0]])]});}
            var Q34;
            {var subQ5=sQuery(id+"F0.wireOp",EDGE,"E49");Q34=makeQuery(id+"F0.imprint","IMPRINT",FACE,{"disambiguationData":[TD([[makeQuery(id+"F0.imprint","IMPRINT",EDGE,{"derivedFrom":subQ5}),1.0]])]});}
            extrude(context, id + "F2", {"entities" : qUnion([Q0, Q1, Q2, Q3, Q4, Q5, Q6, Q7, Q8, Q9, Q10, Q11, Q12, Q13, Q14, Q15, Q16, Q17, Q18, Q19, Q20, Q21, Q22, Q23, Q24, Q25, Q26, Q27, Q28, Q29, Q30, Q31, Q32, Q33, Q34]), "operationType" : NewBodyOperationType.ADD, "depth" : 1000 * mm});
        }
        {
            var Q0;
            {var subQ2=sQuery(id+"F0.wireOp",EDGE,"E20.bottom");Q0=makeQuery(id+"F0.imprint","IMPRINT",FACE,{"disambiguationData":[TD([[makeQuery(id+"F0.imprint","IMPRINT",EDGE,{"derivedFrom":subQ2}),1.0]])]});}
            var Q1;
            {var subQ3=sQuery(id+"F0.wireOp",EDGE,"E59");Q1=makeQuery(id+"F0.imprint","IMPRINT",FACE,{"disambiguationData":[TD([[makeQuery(id+"F0.imprint","IMPRINT",EDGE,{"derivedFrom":subQ3}),1.0]])]});}
            var Q2;
            {var subQ0=sQuery(id+"F0.wireOp",EDGE,"E59");Q2=makeQuery(id+"F0.imprint","IMPRINT",FACE,{"disambiguationData":[TD([[makeQuery(id+"F0.imprint","IMPRINT",EDGE,{"derivedFrom":subQ0}),-1.0]])]});}
            var Q3;
            {var subQ1=sQuery(id+"F0.wireOp",EDGE,"E14.top");Q3=makeQuery(id+"F0.imprint","IMPRINT",FACE,{"disambiguationData":[TD([[makeQuery(id+"F0.imprint","IMPRINT",EDGE,{"derivedFrom":subQ1}),1.0]])]});}
            var Q4;
            {var subQ3=sQuery(id+"F0.wireOp",EDGE,"E35.right");Q4=makeQuery(id+"F0.imprint","IMPRINT",FACE,{"disambiguationData":[TD([[makeQuery(id+"F0.imprint","IMPRINT",EDGE,{"derivedFrom":subQ3}),-1.0]])]});}
            var Q5;
            {var subQ3=sQuery(id+"F0.wireOp",EDGE,"E52");Q5=makeQuery(id+"F0.imprint","IMPRINT",FACE,{"disambiguationData":[TD([[makeQuery(id+"F0.imprint","IMPRINT",EDGE,{"derivedFrom":subQ3}),1.0]])]});}
            var Q6;
            {var subQ7=sQuery(id+"F0.wireOp",EDGE,"E43");Q6=makeQuery(id+"F0.imprint","IMPRINT",FACE,{"disambiguationData":[TD([[makeQuery(id+"F0.imprint","IMPRINT",EDGE,{"derivedFrom":subQ7}),1.0]])]});}
            var Q7;
            Q7=makeQuery(id+"F0.imprint","IMPRINT",FACE,{"disambiguationData":[TD([[makeQuery(id+"F0.imprint","IMPRINT",EDGE,{"derivedFrom":sQuery(id+"F0.wireOp",EDGE,"E3.top")}),-1.0]])]});
            var Q8;
            {var subQ5=sQuery(id+"F0.wireOp",EDGE,"E54");Q8=makeQuery(id+"F0.imprint","IMPRINT",FACE,{"disambiguationData":[TD([[makeQuery(id+"F0.imprint","IMPRINT",EDGE,{"derivedFrom":subQ5}),-1.0]])]});}
            var Q9;
            {var subQ4=sQuery(id+"F0.wireOp",EDGE,"E53");Q9=makeQuery(id+"F0.imprint","IMPRINT",FACE,{"disambiguationData":[TD([[makeQuery(id+"F0.imprint","IMPRINT",EDGE,{"derivedFrom":subQ4}),1.0]])]});}
            var Q10;
            {var subQ0=sQuery(id+"F0.wireOp",EDGE,"E17.bottom");Q10=makeQuery(id+"F0.imprint","IMPRINT",FACE,{"disambiguationData":[TD([[makeQuery(id+"F0.imprint","IMPRINT",EDGE,{"derivedFrom":subQ0}),1.0]])]});}
            var Q11;
            {var subQ3=sQuery(id+"F0.wireOp",EDGE,"E56");Q11=makeQuery(id+"F0.imprint","IMPRINT",FACE,{"disambiguationData":[TD([[makeQuery(id+"F0.imprint","IMPRINT",EDGE,{"derivedFrom":subQ3}),1.0]])]});}
            var Q12;
            {var subQ4=sQuery(id+"F0.wireOp",EDGE,"E15.top");var subQ6=sQuery(id+"F0.wireOp",EDGE,"E15.left");var subQ7=makeQuery(id+"F0.imprint","INTERSECT",VERTEX,{"derivedFrom":[subQ4,subQ6]});Q12=makeQuery(id+"F0.imprint","IMPRINT",FACE,{"disambiguationData":[TD([[makeQuery(id+"F0.imprint","IMPRINT",EDGE,{"disambiguationData":[TD([[subQ7,-1.0]])],"derivedFrom":subQ4}),1.0]])]});}
            var Q13;
            Q13=makeQuery(id+"F0.imprint","IMPRINT",FACE,{"disambiguationData":[TD([[makeQuery(id+"F0.imprint","IMPRINT",EDGE,{"derivedFrom":sQuery(id+"F0.wireOp",EDGE,"E16.right")}),1.0]])]});
            var Q14;
            {var subQ1=sQuery(id+"F0.wireOp",EDGE,"E29.right");Q14=makeQuery(id+"F0.imprint","IMPRINT",FACE,{"disambiguationData":[TD([[makeQuery(id+"F0.imprint","IMPRINT",EDGE,{"derivedFrom":subQ1}),-1.0]])]});}
            var Q15;
            Q15=makeQuery(id+"F0.imprint","IMPRINT",FACE,{"disambiguationData":[TD([[makeQuery(id+"F0.imprint","IMPRINT",EDGE,{"derivedFrom":sQuery(id+"F0.wireOp",EDGE,"E39.top")}),-1.0]])]});
            var Q16;
            {var subQ1=sQuery(id+"F0.wireOp",EDGE,"E1.top");Q16=makeQuery(id+"F0.imprint","IMPRINT",FACE,{"disambiguationData":[TD([[makeQuery(id+"F0.imprint","IMPRINT",EDGE,{"derivedFrom":subQ1}),-1.0]])]});}
            var Q17;
            {var subQ4=sQuery(id+"F0.wireOp",EDGE,"E1.top");Q17=makeQuery(id+"F0.imprint","IMPRINT",FACE,{"disambiguationData":[TD([[makeQuery(id+"F0.imprint","IMPRINT",EDGE,{"derivedFrom":subQ4}),1.0]])]});}
            var Q18;
            {var subQ0=sQuery(id+"F0.wireOp",EDGE,"E57");Q18=makeQuery(id+"F0.imprint","IMPRINT",FACE,{"disambiguationData":[TD([[makeQuery(id+"F0.imprint","IMPRINT",EDGE,{"derivedFrom":subQ0}),-1.0]])]});}
            var Q19;
            {var subQ0=sQuery(id+"F0.wireOp",EDGE,"E57");Q19=makeQuery(id+"F0.imprint","IMPRINT",FACE,{"disambiguationData":[TD([[makeQuery(id+"F0.imprint","IMPRINT",EDGE,{"derivedFrom":subQ0}),1.0]])]});}
            var Q20;
            {var subQ0=sQuery(id+"F0.wireOp",EDGE,"E26.top");var subQ5=sQuery(id+"F0.wireOp",EDGE,"E21.trimOffspring");var subQ6=makeQuery(id+"F0.imprint","INTERSECT",VERTEX,{"derivedFrom":[subQ5,subQ0]});Q20=makeQuery(id+"F0.imprint","IMPRINT",FACE,{"disambiguationData":[TD([[makeQuery(id+"F0.imprint","IMPRINT",EDGE,{"disambiguationData":[TD([[subQ6,-1.0]])],"derivedFrom":subQ5}),1.0]])]});}
            var Q21;
            {var subQ5=sQuery(id+"F0.wireOp",EDGE,"E68");Q21=makeQuery(id+"F0.imprint","IMPRINT",FACE,{"disambiguationData":[TD([[makeQuery(id+"F0.imprint","IMPRINT",EDGE,{"derivedFrom":subQ5}),-1.0]])]});}
            var Q22;
            {var subQ0=sQuery(id+"F0.wireOp",EDGE,"E28.trimOffspring");var subQ1=sQuery(id+"F0.wireOp",EDGE,"E15.right");var subQ2=makeQuery(id+"F0.imprint","INTERSECT",VERTEX,{"derivedFrom":[subQ1,subQ0]});Q22=makeQuery(id+"F0.imprint","IMPRINT",FACE,{"disambiguationData":[TD([[makeQuery(id+"F0.imprint","IMPRINT",EDGE,{"disambiguationData":[TD([[subQ2,1.0]])],"derivedFrom":subQ1}),-1.0]])]});}
            var Q23;
            {var subQ0=sQuery(id+"F0.wireOp",EDGE,"E26.top");var subQ1=sQuery(id+"F0.wireOp",EDGE,"E21.trimOffspring");var subQ2=makeQuery(id+"F0.imprint","INTERSECT",VERTEX,{"derivedFrom":[subQ1,subQ0]});Q23=makeQuery(id+"F0.imprint","IMPRINT",FACE,{"disambiguationData":[TD([[makeQuery(id+"F0.imprint","IMPRINT",EDGE,{"disambiguationData":[TD([[subQ2,-1.0]])],"derivedFrom":subQ1}),-1.0]])]});}
            var Q24;
            {var subQ0=sQuery(id+"F0.wireOp",EDGE,"E28.trimOffspring");var subQ1=sQuery(id+"F0.wireOp",EDGE,"E21.trimOffspring");var subQ2=makeQuery(id+"F0.imprint","INTERSECT",VERTEX,{"derivedFrom":[subQ1,subQ0]});Q24=makeQuery(id+"F0.imprint","IMPRINT",FACE,{"disambiguationData":[TD([[makeQuery(id+"F0.imprint","IMPRINT",EDGE,{"disambiguationData":[TD([[subQ2,1.0]])],"derivedFrom":subQ1}),-1.0]])]});}
            var Q25;
            {var subQ1=sQuery(id+"F0.wireOp",EDGE,"E15.top");var subQ6=makeQuery(id+"F0.imprint","INTERSECT",VERTEX,{"derivedFrom":[subQ1,sQuery(id+"F0.wireOp",EDGE,"E34")]});Q25=makeQuery(id+"F0.imprint","IMPRINT",FACE,{"disambiguationData":[TD([[makeQuery(id+"F0.imprint","IMPRINT",EDGE,{"disambiguationData":[TD([[subQ6,1.0]])],"derivedFrom":subQ1}),1.0]])]});}
            var Q26;
            {var subQ4=sQuery(id+"F0.wireOp",EDGE,"E0.bottom");Q26=makeQuery(id+"F0.imprint","IMPRINT",FACE,{"disambiguationData":[TD([[makeQuery(id+"F0.imprint","IMPRINT",EDGE,{"derivedFrom":subQ4}),1.0]])]});}
            var Q27;
            {var subQ0=sQuery(id+"F0.wireOp",EDGE,"E63");Q27=makeQuery(id+"F0.imprint","IMPRINT",FACE,{"disambiguationData":[TD([[makeQuery(id+"F0.imprint","IMPRINT",EDGE,{"derivedFrom":subQ0}),-1.0]])]});}
            var Q28;
            {var subQ0=sQuery(id+"F0.wireOp",EDGE,"E31");Q28=makeQuery(id+"F0.imprint","IMPRINT",FACE,{"disambiguationData":[TD([[makeQuery(id+"F0.imprint","IMPRINT",EDGE,{"derivedFrom":subQ0}),1.0]])]});}
            var Q29;
            {var subQ0=sQuery(id+"F0.wireOp",EDGE,"E48");Q29=makeQuery(id+"F0.imprint","IMPRINT",FACE,{"disambiguationData":[TD([[makeQuery(id+"F0.imprint","IMPRINT",EDGE,{"derivedFrom":subQ0}),-1.0]])]});}
            var Q30;
            {var subQ5=sQuery(id+"F0.wireOp",EDGE,"E49");Q30=makeQuery(id+"F0.imprint","IMPRINT",FACE,{"disambiguationData":[TD([[makeQuery(id+"F0.imprint","IMPRINT",EDGE,{"derivedFrom":subQ5}),1.0]])]});}
            extrude(context, id + "F3", {"entities" : qUnion([Q0, Q1, Q2, Q3, Q4, Q5, Q6, Q7, Q8, Q9, Q10, Q11, Q12, Q13, Q14, Q15, Q16, Q17, Q18, Q19, Q20, Q21, Q22, Q23, Q24, Q25, Q26, Q27, Q28, Q29, Q30]), "depth" : 1250 * mm, "hasSecondDirection" : true, "secondDirectionBound" : SecondDirectionBoundingType.UP_TO_NEXT, "secondDirectionOppositeDirection" : false, "secondDirectionDepth" : 1100 * mm});
        }
        {
            var Q0;
            {var subQ1=sQuery(id+"F0.wireOp",EDGE,"E14.top");Q0=makeQuery(id+"F0.imprint","IMPRINT",FACE,{"disambiguationData":[TD([[makeQuery(id+"F0.imprint","IMPRINT",EDGE,{"derivedFrom":subQ1}),1.0]])]});}
            var Q1;
            {var subQ3=sQuery(id+"F0.wireOp",EDGE,"E59");Q1=makeQuery(id+"F0.imprint","IMPRINT",FACE,{"disambiguationData":[TD([[makeQuery(id+"F0.imprint","IMPRINT",EDGE,{"derivedFrom":subQ3}),1.0]])]});}
            var Q2;
            {var subQ2=sQuery(id+"F0.wireOp",EDGE,"E20.bottom");Q2=makeQuery(id+"F0.imprint","IMPRINT",FACE,{"disambiguationData":[TD([[makeQuery(id+"F0.imprint","IMPRINT",EDGE,{"derivedFrom":subQ2}),1.0]])]});}
            var Q3;
            {var subQ3=sQuery(id+"F0.wireOp",EDGE,"E35.right");Q3=makeQuery(id+"F0.imprint","IMPRINT",FACE,{"disambiguationData":[TD([[makeQuery(id+"F0.imprint","IMPRINT",EDGE,{"derivedFrom":subQ3}),-1.0]])]});}
            var Q4;
            {var subQ3=sQuery(id+"F0.wireOp",EDGE,"E52");Q4=makeQuery(id+"F0.imprint","IMPRINT",FACE,{"disambiguationData":[TD([[makeQuery(id+"F0.imprint","IMPRINT",EDGE,{"derivedFrom":subQ3}),1.0]])]});}
            var Q5;
            {var subQ7=sQuery(id+"F0.wireOp",EDGE,"E43");Q5=makeQuery(id+"F0.imprint","IMPRINT",FACE,{"disambiguationData":[TD([[makeQuery(id+"F0.imprint","IMPRINT",EDGE,{"derivedFrom":subQ7}),1.0]])]});}
            var Q6;
            {var subQ5=sQuery(id+"F0.wireOp",EDGE,"E49");Q6=makeQuery(id+"F0.imprint","IMPRINT",FACE,{"disambiguationData":[TD([[makeQuery(id+"F0.imprint","IMPRINT",EDGE,{"derivedFrom":subQ5}),1.0]])]});}
            var Q7;
            {var subQ0=sQuery(id+"F0.wireOp",EDGE,"E48");Q7=makeQuery(id+"F0.imprint","IMPRINT",FACE,{"disambiguationData":[TD([[makeQuery(id+"F0.imprint","IMPRINT",EDGE,{"derivedFrom":subQ0}),-1.0]])]});}
            var Q8;
            {var subQ5=sQuery(id+"F0.wireOp",EDGE,"E54");Q8=makeQuery(id+"F0.imprint","IMPRINT",FACE,{"disambiguationData":[TD([[makeQuery(id+"F0.imprint","IMPRINT",EDGE,{"derivedFrom":subQ5}),-1.0]])]});}
            var Q9;
            {var subQ4=sQuery(id+"F0.wireOp",EDGE,"E53");Q9=makeQuery(id+"F0.imprint","IMPRINT",FACE,{"disambiguationData":[TD([[makeQuery(id+"F0.imprint","IMPRINT",EDGE,{"derivedFrom":subQ4}),1.0]])]});}
            var Q10;
            {var subQ0=sQuery(id+"F0.wireOp",EDGE,"E17.bottom");Q10=makeQuery(id+"F0.imprint","IMPRINT",FACE,{"disambiguationData":[TD([[makeQuery(id+"F0.imprint","IMPRINT",EDGE,{"derivedFrom":subQ0}),1.0]])]});}
            var Q11;
            Q11=makeQuery(id+"F0.imprint","IMPRINT",FACE,{"disambiguationData":[TD([[makeQuery(id+"F0.imprint","IMPRINT",EDGE,{"derivedFrom":sQuery(id+"F0.wireOp",EDGE,"E16.right")}),1.0]])]});
            var Q12;
            {var subQ1=sQuery(id+"F0.wireOp",EDGE,"E29.right");Q12=makeQuery(id+"F0.imprint","IMPRINT",FACE,{"disambiguationData":[TD([[makeQuery(id+"F0.imprint","IMPRINT",EDGE,{"derivedFrom":subQ1}),-1.0]])]});}
            var Q13;
            Q13=makeQuery(id+"F0.imprint","IMPRINT",FACE,{"disambiguationData":[TD([[makeQuery(id+"F0.imprint","IMPRINT",EDGE,{"derivedFrom":sQuery(id+"F0.wireOp",EDGE,"E39.top")}),-1.0]])]});
            var Q14;
            {var subQ1=sQuery(id+"F0.wireOp",EDGE,"E1.top");Q14=makeQuery(id+"F0.imprint","IMPRINT",FACE,{"disambiguationData":[TD([[makeQuery(id+"F0.imprint","IMPRINT",EDGE,{"derivedFrom":subQ1}),-1.0]])]});}
            var Q15;
            {var subQ4=sQuery(id+"F0.wireOp",EDGE,"E1.top");Q15=makeQuery(id+"F0.imprint","IMPRINT",FACE,{"disambiguationData":[TD([[makeQuery(id+"F0.imprint","IMPRINT",EDGE,{"derivedFrom":subQ4}),1.0]])]});}
            var Q16;
            {var subQ3=sQuery(id+"F0.wireOp",EDGE,"E56");Q16=makeQuery(id+"F0.imprint","IMPRINT",FACE,{"disambiguationData":[TD([[makeQuery(id+"F0.imprint","IMPRINT",EDGE,{"derivedFrom":subQ3}),1.0]])]});}
            var Q17;
            {var subQ4=sQuery(id+"F0.wireOp",EDGE,"E15.top");var subQ6=sQuery(id+"F0.wireOp",EDGE,"E15.left");var subQ7=makeQuery(id+"F0.imprint","INTERSECT",VERTEX,{"derivedFrom":[subQ4,subQ6]});Q17=makeQuery(id+"F0.imprint","IMPRINT",FACE,{"disambiguationData":[TD([[makeQuery(id+"F0.imprint","IMPRINT",EDGE,{"disambiguationData":[TD([[subQ7,-1.0]])],"derivedFrom":subQ4}),1.0]])]});}
            var Q18;
            {var subQ1=sQuery(id+"F0.wireOp",EDGE,"E15.top");var subQ6=makeQuery(id+"F0.imprint","INTERSECT",VERTEX,{"derivedFrom":[subQ1,sQuery(id+"F0.wireOp",EDGE,"E34")]});Q18=makeQuery(id+"F0.imprint","IMPRINT",FACE,{"disambiguationData":[TD([[makeQuery(id+"F0.imprint","IMPRINT",EDGE,{"disambiguationData":[TD([[subQ6,1.0]])],"derivedFrom":subQ1}),1.0]])]});}
            var Q19;
            {var subQ0=sQuery(id+"F0.wireOp",EDGE,"E28.trimOffspring");var subQ1=sQuery(id+"F0.wireOp",EDGE,"E15.right");var subQ2=makeQuery(id+"F0.imprint","INTERSECT",VERTEX,{"derivedFrom":[subQ1,subQ0]});Q19=makeQuery(id+"F0.imprint","IMPRINT",FACE,{"disambiguationData":[TD([[makeQuery(id+"F0.imprint","IMPRINT",EDGE,{"disambiguationData":[TD([[subQ2,1.0]])],"derivedFrom":subQ1}),-1.0]])]});}
            var Q20;
            {var subQ0=sQuery(id+"F0.wireOp",EDGE,"E28.trimOffspring");var subQ1=sQuery(id+"F0.wireOp",EDGE,"E21.trimOffspring");var subQ2=makeQuery(id+"F0.imprint","INTERSECT",VERTEX,{"derivedFrom":[subQ1,subQ0]});Q20=makeQuery(id+"F0.imprint","IMPRINT",FACE,{"disambiguationData":[TD([[makeQuery(id+"F0.imprint","IMPRINT",EDGE,{"disambiguationData":[TD([[subQ2,1.0]])],"derivedFrom":subQ1}),-1.0]])]});}
            var Q21;
            {var subQ0=sQuery(id+"F0.wireOp",EDGE,"E26.top");var subQ1=sQuery(id+"F0.wireOp",EDGE,"E21.trimOffspring");var subQ2=makeQuery(id+"F0.imprint","INTERSECT",VERTEX,{"derivedFrom":[subQ1,subQ0]});Q21=makeQuery(id+"F0.imprint","IMPRINT",FACE,{"disambiguationData":[TD([[makeQuery(id+"F0.imprint","IMPRINT",EDGE,{"disambiguationData":[TD([[subQ2,-1.0]])],"derivedFrom":subQ1}),-1.0]])]});}
            var Q22;
            {var subQ0=sQuery(id+"F0.wireOp",EDGE,"E26.top");var subQ5=sQuery(id+"F0.wireOp",EDGE,"E21.trimOffspring");var subQ6=makeQuery(id+"F0.imprint","INTERSECT",VERTEX,{"derivedFrom":[subQ5,subQ0]});Q22=makeQuery(id+"F0.imprint","IMPRINT",FACE,{"disambiguationData":[TD([[makeQuery(id+"F0.imprint","IMPRINT",EDGE,{"disambiguationData":[TD([[subQ6,-1.0]])],"derivedFrom":subQ5}),1.0]])]});}
            var Q23;
            {var subQ0=sQuery(id+"F0.wireOp",EDGE,"E57");Q23=makeQuery(id+"F0.imprint","IMPRINT",FACE,{"disambiguationData":[TD([[makeQuery(id+"F0.imprint","IMPRINT",EDGE,{"derivedFrom":subQ0}),1.0]])]});}
            var Q24;
            {var subQ5=sQuery(id+"F0.wireOp",EDGE,"E68");Q24=makeQuery(id+"F0.imprint","IMPRINT",FACE,{"disambiguationData":[TD([[makeQuery(id+"F0.imprint","IMPRINT",EDGE,{"derivedFrom":subQ5}),-1.0]])]});}
            var Q25;
            {var subQ0=sQuery(id+"F0.wireOp",EDGE,"E31");Q25=makeQuery(id+"F0.imprint","IMPRINT",FACE,{"disambiguationData":[TD([[makeQuery(id+"F0.imprint","IMPRINT",EDGE,{"derivedFrom":subQ0}),1.0]])]});}
            var Q26;
            {var subQ0=sQuery(id+"F0.wireOp",EDGE,"E63");Q26=makeQuery(id+"F0.imprint","IMPRINT",FACE,{"disambiguationData":[TD([[makeQuery(id+"F0.imprint","IMPRINT",EDGE,{"derivedFrom":subQ0}),-1.0]])]});}
            var Q27;
            {var subQ4=sQuery(id+"F0.wireOp",EDGE,"E0.bottom");Q27=makeQuery(id+"F0.imprint","IMPRINT",FACE,{"disambiguationData":[TD([[makeQuery(id+"F0.imprint","IMPRINT",EDGE,{"derivedFrom":subQ4}),1.0]])]});}
            var Q28;
            Q28=makeQuery(id+"F0.imprint","IMPRINT",FACE,{"disambiguationData":[TD([[makeQuery(id+"F0.imprint","IMPRINT",EDGE,{"derivedFrom":sQuery(id+"F0.wireOp",EDGE,"E3.top")}),-1.0]])]});
            var Q29;
            Q29=makeQuery(id+"F2.opExtrude","CAP_FACE",FACE,{"disambiguationData":[OSD([sQuery(id+"F0.wireOp",EDGE,"E3.top"),sQuery(id+"F0.wireOp",EDGE,"E4.left"),sQuery(id+"F0.wireOp",EDGE,"E4.right"),sQuery(id+"F0.wireOp",EDGE,"E5.left"),sQuery(id+"F0.wireOp",EDGE,"E5.right"),sQuery(id+"F0.wireOp",EDGE,"E6.right"),sQuery(id+"F0.wireOp",EDGE,"E8.trimOffspring"),sQuery(id+"F0.wireOp",EDGE,"E11.trimOffspring"),sQuery(id+"F0.wireOp",EDGE,"E13.bottom"),sQuery(id+"F0.wireOp",EDGE,"E13.top"),sQuery(id+"F0.wireOp",EDGE,"E13.left"),sQuery(id+"F0.wireOp",EDGE,"E14.bottom"),sQuery(id+"F0.wireOp",EDGE,"E14.top"),sQuery(id+"F0.wireOp",EDGE,"E14.left"),sQuery(id+"F0.wireOp",EDGE,"E15.bottom"),sQuery(id+"F0.wireOp",EDGE,"E15.left"),sQuery(id+"F0.wireOp",EDGE,"E20.bottom"),sQuery(id+"F0.wireOp",EDGE,"E20.top"),sQuery(id+"F0.wireOp",EDGE,"E19.right"),sQuery(id+"F0.wireOp",EDGE,"E22.trimOffspring"),sQuery(id+"F0.wireOp",EDGE,"E23.trimOffspring"),sQuery(id+"F0.wireOp",EDGE,"E35.top"),sQuery(id+"F0.wireOp",EDGE,"E35.right"),sQuery(id+"F0.wireOp",EDGE,"E36.bottom"),sQuery(id+"F0.wireOp",EDGE,"E36.top"),sQuery(id+"F0.wireOp",EDGE,"E36.left"),sQuery(id+"F0.wireOp",EDGE,"E36.right"),sQuery(id+"F0.wireOp",EDGE,"E37"),sQuery(id+"F0.wireOp",EDGE,"E48"),sQuery(id+"F0.wireOp",EDGE,"E51"),sQuery(id+"F0.wireOp",EDGE,"E52"),sQuery(id+"F0.wireOp",EDGE,"E54")])],"isStart":false});
            extrude(context, id + "F4", {"entities" : qUnion([Q0, Q1, Q2, Q3, Q4, Q5, Q6, Q7, Q8, Q9, Q10, Q11, Q12, Q13, Q14, Q15, Q16, Q17, Q18, Q19, Q20, Q21, Q22, Q23, Q24, Q25, Q26, Q27, Q28]), "depth" : 2000 * mm, "hasSecondDirection" : true, "secondDirectionOppositeDirection" : false, "secondDirectionBoundEntityFace" : qUnion([Q29]), "secondDirectionDepth" : 1250 * mm});
        }
        {
            var Q0;
            {var subQ1=sQuery(id+"F0.wireOp",EDGE,"E14.top");Q0=makeQuery(id+"F0.imprint","IMPRINT",FACE,{"disambiguationData":[TD([[makeQuery(id+"F0.imprint","IMPRINT",EDGE,{"derivedFrom":subQ1}),1.0]])]});}
            var Q1;
            {var subQ3=sQuery(id+"F0.wireOp",EDGE,"E35.right");Q1=makeQuery(id+"F0.imprint","IMPRINT",FACE,{"disambiguationData":[TD([[makeQuery(id+"F0.imprint","IMPRINT",EDGE,{"derivedFrom":subQ3}),-1.0]])]});}
            var Q2;
            {var subQ0=sQuery(id+"F0.wireOp",EDGE,"E59");Q2=makeQuery(id+"F0.imprint","IMPRINT",FACE,{"disambiguationData":[TD([[makeQuery(id+"F0.imprint","IMPRINT",EDGE,{"derivedFrom":subQ0}),-1.0]])]});}
            var Q3;
            {var subQ3=sQuery(id+"F0.wireOp",EDGE,"E59");Q3=makeQuery(id+"F0.imprint","IMPRINT",FACE,{"disambiguationData":[TD([[makeQuery(id+"F0.imprint","IMPRINT",EDGE,{"derivedFrom":subQ3}),1.0]])]});}
            var Q4;
            {var subQ2=sQuery(id+"F0.wireOp",EDGE,"E20.bottom");Q4=makeQuery(id+"F0.imprint","IMPRINT",FACE,{"disambiguationData":[TD([[makeQuery(id+"F0.imprint","IMPRINT",EDGE,{"derivedFrom":subQ2}),1.0]])]});}
            var Q5;
            {var subQ0=sQuery(id+"F0.wireOp",EDGE,"E42");Q5=makeQuery(id+"F0.imprint","IMPRINT",FACE,{"disambiguationData":[TD([[makeQuery(id+"F0.imprint","IMPRINT",EDGE,{"derivedFrom":subQ0}),1.0]])]});}
            var Q6;
            {var subQ7=sQuery(id+"F0.wireOp",EDGE,"E43");Q6=makeQuery(id+"F0.imprint","IMPRINT",FACE,{"disambiguationData":[TD([[makeQuery(id+"F0.imprint","IMPRINT",EDGE,{"derivedFrom":subQ7}),1.0]])]});}
            var Q7;
            {var subQ0=sQuery(id+"F0.wireOp",EDGE,"E44");Q7=makeQuery(id+"F0.imprint","IMPRINT",FACE,{"disambiguationData":[TD([[makeQuery(id+"F0.imprint","IMPRINT",EDGE,{"derivedFrom":subQ0}),-1.0]])]});}
            var Q8;
            Q8=makeQuery(id+"F0.imprint","IMPRINT",FACE,{"disambiguationData":[TD([[makeQuery(id+"F0.imprint","IMPRINT",EDGE,{"derivedFrom":sQuery(id+"F0.wireOp",EDGE,"E3.top")}),-1.0]])]});
            var Q9;
            {var subQ5=sQuery(id+"F0.wireOp",EDGE,"E49");Q9=makeQuery(id+"F0.imprint","IMPRINT",FACE,{"disambiguationData":[TD([[makeQuery(id+"F0.imprint","IMPRINT",EDGE,{"derivedFrom":subQ5}),1.0]])]});}
            var Q10;
            {var subQ0=sQuery(id+"F0.wireOp",EDGE,"E48");Q10=makeQuery(id+"F0.imprint","IMPRINT",FACE,{"disambiguationData":[TD([[makeQuery(id+"F0.imprint","IMPRINT",EDGE,{"derivedFrom":subQ0}),1.0]])]});}
            var Q11;
            {var subQ0=sQuery(id+"F0.wireOp",EDGE,"E48");Q11=makeQuery(id+"F0.imprint","IMPRINT",FACE,{"disambiguationData":[TD([[makeQuery(id+"F0.imprint","IMPRINT",EDGE,{"derivedFrom":subQ0}),-1.0]])]});}
            var Q12;
            {var subQ0=sQuery(id+"F0.wireOp",EDGE,"E51");Q12=makeQuery(id+"F0.imprint","IMPRINT",FACE,{"disambiguationData":[TD([[makeQuery(id+"F0.imprint","IMPRINT",EDGE,{"derivedFrom":subQ0}),1.0]])]});}
            var Q13;
            {var subQ3=sQuery(id+"F0.wireOp",EDGE,"E52");Q13=makeQuery(id+"F0.imprint","IMPRINT",FACE,{"disambiguationData":[TD([[makeQuery(id+"F0.imprint","IMPRINT",EDGE,{"derivedFrom":subQ3}),1.0]])]});}
            var Q14;
            {var subQ4=sQuery(id+"F0.wireOp",EDGE,"E0.bottom");Q14=makeQuery(id+"F0.imprint","IMPRINT",FACE,{"disambiguationData":[TD([[makeQuery(id+"F0.imprint","IMPRINT",EDGE,{"derivedFrom":subQ4}),1.0]])]});}
            var Q15;
            {var subQ4=sQuery(id+"F0.wireOp",EDGE,"E1.top");Q15=makeQuery(id+"F0.imprint","IMPRINT",FACE,{"disambiguationData":[TD([[makeQuery(id+"F0.imprint","IMPRINT",EDGE,{"derivedFrom":subQ4}),1.0]])]});}
            var Q16;
            {var subQ0=sQuery(id+"F0.wireOp",EDGE,"E63");Q16=makeQuery(id+"F0.imprint","IMPRINT",FACE,{"disambiguationData":[TD([[makeQuery(id+"F0.imprint","IMPRINT",EDGE,{"derivedFrom":subQ0}),-1.0]])]});}
            var Q17;
            {var subQ0=sQuery(id+"F0.wireOp",EDGE,"E63");Q17=makeQuery(id+"F0.imprint","IMPRINT",FACE,{"disambiguationData":[TD([[makeQuery(id+"F0.imprint","IMPRINT",EDGE,{"derivedFrom":subQ0}),1.0]])]});}
            var Q18;
            {var subQ1=sQuery(id+"F0.wireOp",EDGE,"E1.top");Q18=makeQuery(id+"F0.imprint","IMPRINT",FACE,{"disambiguationData":[TD([[makeQuery(id+"F0.imprint","IMPRINT",EDGE,{"derivedFrom":subQ1}),-1.0]])]});}
            var Q19;
            {var subQ0=sQuery(id+"F0.wireOp",EDGE,"E68");Q19=makeQuery(id+"F0.imprint","IMPRINT",FACE,{"disambiguationData":[TD([[makeQuery(id+"F0.imprint","IMPRINT",EDGE,{"derivedFrom":subQ0}),1.0]])]});}
            var Q20;
            {var subQ5=sQuery(id+"F0.wireOp",EDGE,"E68");Q20=makeQuery(id+"F0.imprint","IMPRINT",FACE,{"disambiguationData":[TD([[makeQuery(id+"F0.imprint","IMPRINT",EDGE,{"derivedFrom":subQ5}),-1.0]])]});}
            var Q21;
            {var subQ0=sQuery(id+"F0.wireOp",EDGE,"E26.top");var subQ5=sQuery(id+"F0.wireOp",EDGE,"E21.trimOffspring");var subQ6=makeQuery(id+"F0.imprint","INTERSECT",VERTEX,{"derivedFrom":[subQ5,subQ0]});Q21=makeQuery(id+"F0.imprint","IMPRINT",FACE,{"disambiguationData":[TD([[makeQuery(id+"F0.imprint","IMPRINT",EDGE,{"disambiguationData":[TD([[subQ6,-1.0]])],"derivedFrom":subQ5}),1.0]])]});}
            var Q22;
            {var subQ0=sQuery(id+"F0.wireOp",EDGE,"E28.trimOffspring");var subQ1=sQuery(id+"F0.wireOp",EDGE,"E15.right");var subQ2=makeQuery(id+"F0.imprint","INTERSECT",VERTEX,{"derivedFrom":[subQ1,subQ0]});Q22=makeQuery(id+"F0.imprint","IMPRINT",FACE,{"disambiguationData":[TD([[makeQuery(id+"F0.imprint","IMPRINT",EDGE,{"disambiguationData":[TD([[subQ2,1.0]])],"derivedFrom":subQ1}),-1.0]])]});}
            var Q23;
            {var subQ1=sQuery(id+"F0.wireOp",EDGE,"E15.top");var subQ6=makeQuery(id+"F0.imprint","INTERSECT",VERTEX,{"derivedFrom":[subQ1,sQuery(id+"F0.wireOp",EDGE,"E34")]});Q23=makeQuery(id+"F0.imprint","IMPRINT",FACE,{"disambiguationData":[TD([[makeQuery(id+"F0.imprint","IMPRINT",EDGE,{"disambiguationData":[TD([[subQ6,1.0]])],"derivedFrom":subQ1}),1.0]])]});}
            var Q24;
            {var subQ0=sQuery(id+"F0.wireOp",EDGE,"E26.top");var subQ1=sQuery(id+"F0.wireOp",EDGE,"E21.trimOffspring");var subQ2=makeQuery(id+"F0.imprint","INTERSECT",VERTEX,{"derivedFrom":[subQ1,subQ0]});Q24=makeQuery(id+"F0.imprint","IMPRINT",FACE,{"disambiguationData":[TD([[makeQuery(id+"F0.imprint","IMPRINT",EDGE,{"disambiguationData":[TD([[subQ2,-1.0]])],"derivedFrom":subQ1}),-1.0]])]});}
            var Q25;
            {var subQ0=sQuery(id+"F0.wireOp",EDGE,"E31");Q25=makeQuery(id+"F0.imprint","IMPRINT",FACE,{"disambiguationData":[TD([[makeQuery(id+"F0.imprint","IMPRINT",EDGE,{"derivedFrom":subQ0}),1.0]])]});}
            var Q26;
            {var subQ0=sQuery(id+"F0.wireOp",EDGE,"E28.trimOffspring");var subQ1=sQuery(id+"F0.wireOp",EDGE,"E21.trimOffspring");var subQ2=makeQuery(id+"F0.imprint","INTERSECT",VERTEX,{"derivedFrom":[subQ1,subQ0]});Q26=makeQuery(id+"F0.imprint","IMPRINT",FACE,{"disambiguationData":[TD([[makeQuery(id+"F0.imprint","IMPRINT",EDGE,{"disambiguationData":[TD([[subQ2,1.0]])],"derivedFrom":subQ1}),-1.0]])]});}
            var Q27;
            Q27=makeQuery(id+"F0.imprint","IMPRINT",FACE,{"disambiguationData":[TD([[makeQuery(id+"F0.imprint","IMPRINT",EDGE,{"derivedFrom":sQuery(id+"F0.wireOp",EDGE,"E39.top")}),-1.0]])]});
            var Q28;
            {var subQ1=sQuery(id+"F0.wireOp",EDGE,"E29.right");Q28=makeQuery(id+"F0.imprint","IMPRINT",FACE,{"disambiguationData":[TD([[makeQuery(id+"F0.imprint","IMPRINT",EDGE,{"derivedFrom":subQ1}),-1.0]])]});}
            var Q29;
            Q29=makeQuery(id+"F0.imprint","IMPRINT",FACE,{"disambiguationData":[TD([[makeQuery(id+"F0.imprint","IMPRINT",EDGE,{"derivedFrom":sQuery(id+"F0.wireOp",EDGE,"E16.right")}),1.0]])]});
            var Q30;
            {var subQ0=sQuery(id+"F0.wireOp",EDGE,"E57");Q30=makeQuery(id+"F0.imprint","IMPRINT",FACE,{"disambiguationData":[TD([[makeQuery(id+"F0.imprint","IMPRINT",EDGE,{"derivedFrom":subQ0}),-1.0]])]});}
            var Q31;
            {var subQ0=sQuery(id+"F0.wireOp",EDGE,"E57");Q31=makeQuery(id+"F0.imprint","IMPRINT",FACE,{"disambiguationData":[TD([[makeQuery(id+"F0.imprint","IMPRINT",EDGE,{"derivedFrom":subQ0}),1.0]])]});}
            var Q32;
            {var subQ0=sQuery(id+"F0.wireOp",EDGE,"E29.top");Q32=makeQuery(id+"F0.imprint","IMPRINT",FACE,{"disambiguationData":[TD([[makeQuery(id+"F0.imprint","IMPRINT",EDGE,{"derivedFrom":subQ0}),1.0]])]});}
            var Q33;
            Q33=makeQuery(id+"F0.imprint","IMPRINT",FACE,{"disambiguationData":[TD([[makeQuery(id+"F0.imprint","IMPRINT",EDGE,{"derivedFrom":sQuery(id+"F0.wireOp",EDGE,"E2.top")}),-1.0]])]});
            var Q34;
            Q34=makeQuery(id+"F0.imprint","IMPRINT",FACE,{"disambiguationData":[TD([[makeQuery(id+"F0.imprint","IMPRINT",EDGE,{"derivedFrom":sQuery(id+"F0.wireOp",EDGE,"E19.bottom")}),1.0]])]});
            var Q35;
            {var subQ5=sQuery(id+"F0.wireOp",EDGE,"E54");Q35=makeQuery(id+"F0.imprint","IMPRINT",FACE,{"disambiguationData":[TD([[makeQuery(id+"F0.imprint","IMPRINT",EDGE,{"derivedFrom":subQ5}),-1.0]])]});}
            var Q36;
            {var subQ0=sQuery(id+"F0.wireOp",EDGE,"E53");Q36=makeQuery(id+"F0.imprint","IMPRINT",FACE,{"disambiguationData":[TD([[makeQuery(id+"F0.imprint","IMPRINT",EDGE,{"derivedFrom":subQ0}),-1.0]])]});}
            var Q37;
            {var subQ4=sQuery(id+"F0.wireOp",EDGE,"E53");Q37=makeQuery(id+"F0.imprint","IMPRINT",FACE,{"disambiguationData":[TD([[makeQuery(id+"F0.imprint","IMPRINT",EDGE,{"derivedFrom":subQ4}),1.0]])]});}
            var Q38;
            {var subQ0=sQuery(id+"F0.wireOp",EDGE,"E55");Q38=makeQuery(id+"F0.imprint","IMPRINT",FACE,{"disambiguationData":[TD([[makeQuery(id+"F0.imprint","IMPRINT",EDGE,{"derivedFrom":subQ0}),1.0]])]});}
            var Q39;
            {var subQ3=sQuery(id+"F0.wireOp",EDGE,"E56");Q39=makeQuery(id+"F0.imprint","IMPRINT",FACE,{"disambiguationData":[TD([[makeQuery(id+"F0.imprint","IMPRINT",EDGE,{"derivedFrom":subQ3}),1.0]])]});}
            var Q40;
            {var subQ4=sQuery(id+"F0.wireOp",EDGE,"E15.top");var subQ6=sQuery(id+"F0.wireOp",EDGE,"E15.left");var subQ7=makeQuery(id+"F0.imprint","INTERSECT",VERTEX,{"derivedFrom":[subQ4,subQ6]});Q40=makeQuery(id+"F0.imprint","IMPRINT",FACE,{"disambiguationData":[TD([[makeQuery(id+"F0.imprint","IMPRINT",EDGE,{"disambiguationData":[TD([[subQ7,-1.0]])],"derivedFrom":subQ4}),1.0]])]});}
            extrude(context, id + "F5", {"entities" : qUnion([Q0, Q1, Q2, Q3, Q4, Q5, Q6, Q7, Q8, Q9, Q10, Q11, Q12, Q13, Q14, Q15, Q16, Q17, Q18, Q19, Q20, Q21, Q22, Q23, Q24, Q25, Q26, Q27, Q28, Q29, Q30, Q31, Q32, Q33, Q34, Q35, Q36, Q37, Q38, Q39, Q40]), "depth" : 2500 * mm, "hasSecondDirection" : true, "secondDirectionOppositeDirection" : false, "secondDirectionDepth" : 2000 * mm});
        }
        {
            var Q0;
            {var subQ1=sQuery(id+"F0.wireOp",EDGE,"E0.right");Q0=makeQuery(id+"F0.imprint","IMPRINT",FACE,{"disambiguationData":[TD([[makeQuery(id+"F0.imprint","IMPRINT",EDGE,{"derivedFrom":subQ1}),1.0]])]});}
            var Q1;
            {var subQ4=sQuery(id+"F0.wireOp",EDGE,"E16.bottom");Q1=makeQuery(id+"F0.imprint","IMPRINT",FACE,{"disambiguationData":[TD([[makeQuery(id+"F0.imprint","IMPRINT",EDGE,{"derivedFrom":subQ4}),1.0]])]});}
            extrude(context, id + "F6", {"entities" : qUnion([Q0, Q1]), "depth" : 1000 * mm});
        }
        {
            var Q0;
            {var subQ0=sQuery(id+"F0.wireOp",EDGE,"E66");Q0=makeQuery(id+"F0.imprint","IMPRINT",FACE,{"disambiguationData":[TD([[makeQuery(id+"F0.imprint","IMPRINT",EDGE,{"derivedFrom":subQ0}),-1.0]])]});}
            var Q1;
            {var subQ0=sQuery(id+"F0.wireOp",EDGE,"E24.trimOffspring");Q1=makeQuery(id+"F0.imprint","IMPRINT",FACE,{"disambiguationData":[TD([[makeQuery(id+"F0.imprint","IMPRINT",EDGE,{"derivedFrom":subQ0}),-1.0]])]});}
            var Q2;
            {var subQ2=sQuery(id+"F0.wireOp",EDGE,"E6.top");Q2=makeQuery(id+"F0.imprint","IMPRINT",FACE,{"disambiguationData":[TD([[makeQuery(id+"F0.imprint","IMPRINT",EDGE,{"derivedFrom":subQ2}),1.0]])]});}
            extrude(context, id + "F7", {"entities" : qUnion([Q0, Q1, Q2]), "depth" : 1000 * mm, "hasSecondDirection" : true, "secondDirectionOppositeDirection" : true, "secondDirectionDepth" : 10 * mm});
        }
        {
            var Q0;
            {var subQ0=sQuery(id+"F0.wireOp",EDGE,"E66");Q0=makeQuery(id+"F0.imprint","IMPRINT",FACE,{"disambiguationData":[TD([[makeQuery(id+"F0.imprint","IMPRINT",EDGE,{"derivedFrom":subQ0}),-1.0]])]});}
            var Q1;
            {var subQ0=sQuery(id+"F0.wireOp",EDGE,"E66");Q1=makeQuery(id+"F0.imprint","IMPRINT",FACE,{"disambiguationData":[TD([[makeQuery(id+"F0.imprint","IMPRINT",EDGE,{"derivedFrom":subQ0}),1.0]])]});}
            var Q2;
            {var subQ0=sQuery(id+"F0.wireOp",EDGE,"E24.trimOffspring");Q2=makeQuery(id+"F0.imprint","IMPRINT",FACE,{"disambiguationData":[TD([[makeQuery(id+"F0.imprint","IMPRINT",EDGE,{"derivedFrom":subQ0}),-1.0]])]});}
            var Q3;
            {var subQ2=sQuery(id+"F0.wireOp",EDGE,"E6.top");Q3=makeQuery(id+"F0.imprint","IMPRINT",FACE,{"disambiguationData":[TD([[makeQuery(id+"F0.imprint","IMPRINT",EDGE,{"derivedFrom":subQ2}),1.0]])]});}
            extrude(context, id + "F8", {"entities" : qUnion([Q0, Q1, Q2, Q3]), "oppositeDirection" : true, "depth" : 20 * mm, "hasSecondDirection" : true, "secondDirectionOppositeDirection" : true, "secondDirectionDepth" : 10 * mm});
        }
        {
            var Q0;
            {var subQ0=sQuery(id+"F0.wireOp",EDGE,"E66");Q0=makeQuery(id+"F0.imprint","IMPRINT",FACE,{"disambiguationData":[TD([[makeQuery(id+"F0.imprint","IMPRINT",EDGE,{"derivedFrom":subQ0}),-1.0]])]});}
            var Q1;
            {var subQ0=sQuery(id+"F0.wireOp",EDGE,"E24.trimOffspring");Q1=makeQuery(id+"F0.imprint","IMPRINT",FACE,{"disambiguationData":[TD([[makeQuery(id+"F0.imprint","IMPRINT",EDGE,{"derivedFrom":subQ0}),-1.0]])]});}
            var Q2;
            {var subQ2=sQuery(id+"F0.wireOp",EDGE,"E6.top");Q2=makeQuery(id+"F0.imprint","IMPRINT",FACE,{"disambiguationData":[TD([[makeQuery(id+"F0.imprint","IMPRINT",EDGE,{"derivedFrom":subQ2}),1.0]])]});}
            extrude(context, id + "F9", {"entities" : qUnion([Q0, Q1, Q2]), "depth" : 2000 * mm, "hasSecondDirection" : true, "secondDirectionOppositeDirection" : false, "secondDirectionDepth" : 1000 * mm});
        }
        {
            var Q0;
            {var subQ0=sQuery(id+"F0.wireOp",EDGE,"E66");Q0=makeQuery(id+"F0.imprint","IMPRINT",FACE,{"disambiguationData":[TD([[makeQuery(id+"F0.imprint","IMPRINT",EDGE,{"derivedFrom":subQ0}),-1.0]])]});}
            var Q1;
            {var subQ0=sQuery(id+"F0.wireOp",EDGE,"E66");Q1=makeQuery(id+"F0.imprint","IMPRINT",FACE,{"disambiguationData":[TD([[makeQuery(id+"F0.imprint","IMPRINT",EDGE,{"derivedFrom":subQ0}),1.0]])]});}
            var Q2;
            {var subQ0=sQuery(id+"F0.wireOp",EDGE,"E24.trimOffspring");Q2=makeQuery(id+"F0.imprint","IMPRINT",FACE,{"disambiguationData":[TD([[makeQuery(id+"F0.imprint","IMPRINT",EDGE,{"derivedFrom":subQ0}),-1.0]])]});}
            var Q3;
            {var subQ2=sQuery(id+"F0.wireOp",EDGE,"E6.top");Q3=makeQuery(id+"F0.imprint","IMPRINT",FACE,{"disambiguationData":[TD([[makeQuery(id+"F0.imprint","IMPRINT",EDGE,{"derivedFrom":subQ2}),1.0]])]});}
            extrude(context, id + "F10", {"entities" : qUnion([Q0, Q1, Q2, Q3]), "depth" : 2500 * mm, "hasSecondDirection" : true, "secondDirectionOppositeDirection" : false, "secondDirectionDepth" : 2000 * mm});
        }
        {
            var Q0;
            Q0=makeQuery(id+"F1.opExtrude","CAP_FACE",FACE,{"disambiguationData":[OSD([sQuery(id+"F0.wireOp",EDGE,"E1.bottom"),sQuery(id+"F0.wireOp",EDGE,"E1.left"),sQuery(id+"F0.wireOp",EDGE,"E1.right"),sQuery(id+"F0.wireOp",EDGE,"E5.right"),sQuery(id+"F0.wireOp",EDGE,"E12.trimOffspring"),sQuery(id+"F0.wireOp",EDGE,"E13.top"),sQuery(id+"F0.wireOp",EDGE,"E13.left"),sQuery(id+"F0.wireOp",EDGE,"E15.bottom"),sQuery(id+"F0.wireOp",EDGE,"E15.right"),sQuery(id+"F0.wireOp",EDGE,"E26.left"),sQuery(id+"F0.wireOp",EDGE,"E30.top"),sQuery(id+"F0.wireOp",EDGE,"E30.right"),sQuery(id+"F0.wireOp",EDGE,"E39.top"),sQuery(id+"F0.wireOp",EDGE,"E39.left")])],"isStart":true});
            var sketch = newSketch(context, id + "F11", { "sketchPlane" : qUnion([Q0])});
            skArc(sketch, "E71", {"start": v(-900, -600) * mm, "mid": v(1086.5, 1386.5) * mm, "end": v(-900, 3372.98) * mm});
            skArc(sketch, "E72", {"start": v(1086.5, 1386.5) * mm, "mid": v(1548.47, 2018.42) * mm, "end": v(1504.99, 2800) * mm});
            skSolve(sketch);
        }
        {
            var Q0;
            Q0=sQuery(id+"F11.wireOp",EDGE,"E71");
            extrude(context, id + "F12", {"bodyType" : ToolBodyType.SURFACE, "surfaceEntities" : qUnion([Q0]), "depth" : 25 * mm, "offsetDistance" : 25 * mm});
        }
    });
